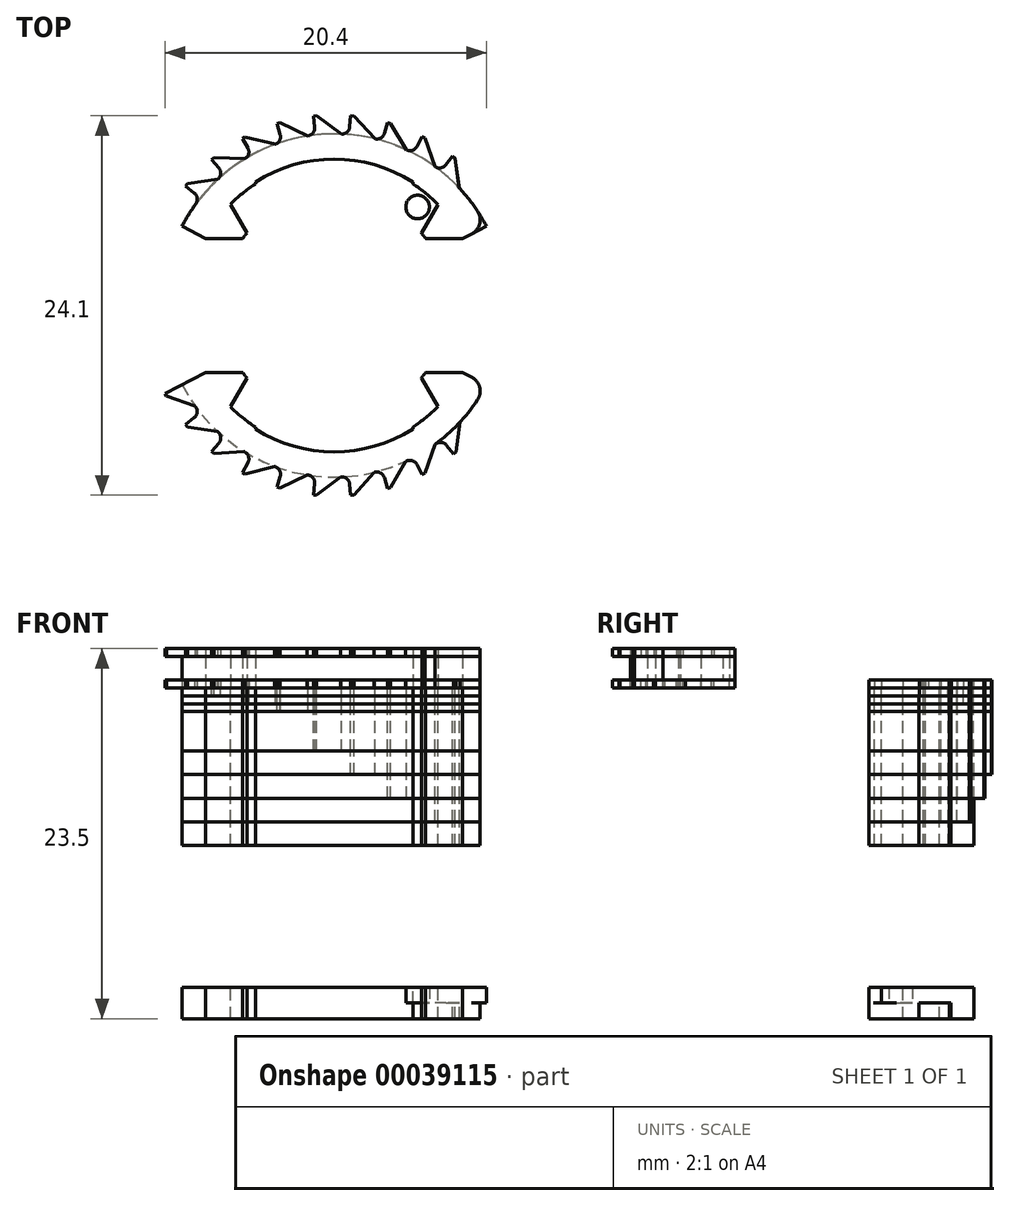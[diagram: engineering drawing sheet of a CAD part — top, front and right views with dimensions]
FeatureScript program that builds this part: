
annotation { "Feature Type Name" : "Feature", "Feature Type Description" : "" }
export const myFeature = defineFeature(function(context is Context, id is Id, definition is map)
    precondition{}
    {
        {
            var Q0;
            Q0=qCreatedBy(makeId("Top.planeOp"),FACE);
            var sketch = newSketch(context, id + "F0", { "sketchPlane" : qUnion([Q0])});
            skArc(sketch, "E0", {"start": v(6.4, -8.83) * mm, "mid": v(-2.5, -10.6) * mm, "end": v(-9.67, -5.03) * mm});
            skArc(sketch, "E1", {"start": v(-5, -7.84) * mm, "mid": v(0, -9.3) * mm, "end": v(5, -7.84) * mm});
            skArc(sketch, "E2", {"start": v(6.6, -6.42) * mm, "mid": v(5.83, -7.12) * mm, "end": v(5, -7.72) * mm});
            skLineSegment(sketch, "E3", {"start": v(9.67, -5.03) * mm, "end": v(0, 0) * mm, "construction": true});
            skLineSegment(sketch, "E4", {"start": v(-9.67, -5.03) * mm, "end": v(0, 0) * mm, "construction": true});
            skLineSegment(sketch, "E5", {"start": v(5, -7.84) * mm, "end": v(5, -7.72) * mm});
            skLineSegment(sketch, "E6", {"start": v(-5, -7.84) * mm, "end": v(-5, -7.72) * mm});
            skArc(sketch, "E7.trimOffspring", {"start": v(-5, -7.72) * mm, "mid": v(-5.83, -7.12) * mm, "end": v(-6.6, -6.42) * mm});
            skArc(sketch, "E8", {"start": v(-6.15, -3.75) * mm, "mid": v(0.86, -7.15) * mm, "end": v(6.86, -2.18) * mm, "construction": true});
            skLineSegment(sketch, "E9", {"start": v(-6.6, -6.42) * mm, "end": v(-5.54, -4.6) * mm});
            skLineSegment(sketch, "E10", {"start": v(6.6, -6.42) * mm, "end": v(5.54, -4.6) * mm});
            skArc(sketch, "E11", {"start": v(-5.54, -4.6) * mm, "mid": v(-5.68, -4.43) * mm, "end": v(-5.81, -4.25) * mm});
            skLineSegment(sketch, "E12", {"start": v(-5.81, -4.25) * mm, "end": v(-8.16, -4.25) * mm});
            skLineSegment(sketch, "E13", {"start": v(-8.16, -4.25) * mm, "end": v(-9.67, -5.03) * mm});
            skArc(sketch, "E14", {"start": v(5.54, -4.6) * mm, "mid": v(5.68, -4.43) * mm, "end": v(5.81, -4.25) * mm});
            skLineSegment(sketch, "E15", {"start": v(5.81, -4.25) * mm, "end": v(8.16, -4.25) * mm});
            skLineSegment(sketch, "E16", {"start": v(8.16, -4.25) * mm, "end": v(8.74, -4.55) * mm});
            skPoint(sketch, "E17.visualSharp", {"position": v(9.67, -5.03) * mm});
            skArc(sketch, "E17.filletArc", {"start": v(9.11, -5.98) * mm, "mid": v(9.24, -5.18) * mm, "end": v(8.74, -4.55) * mm});
            skPoint(sketch, "E18.visualSharp", {"position": v(-9.67, -5.03) * mm});
            skLineSegment(sketch, "E19", {"start": v(5.26, -10.1) * mm, "end": v(5.59, -10.73) * mm});
            skLineSegment(sketch, "E20", {"start": v(5.59, -10.73) * mm, "end": v(5.76, -10.64) * mm});
            skLineSegment(sketch, "E21", {"start": v(5.76, -10.64) * mm, "end": v(6.4, -8.83) * mm});
            skLineSegment(sketch, "E22", {"start": v(6.4, -8.83) * mm, "end": v(7.12, -9.83) * mm, "construction": true});
            skPoint(sketch, "E23.newPointA", {"position": v(5.03, -9.67) * mm});
            skArc(sketch, "E23.filletArc", {"start": v(5.26, -10.1) * mm, "mid": v(4.98, -9.86) * mm, "end": v(4.6, -9.88) * mm});
            skArc(sketch, "E24", {"start": v(9.11, -5.98) * mm, "mid": v(7.88, -7.53) * mm, "end": v(6.4, -8.83) * mm});
            skSolve(sketch);
        }
        {
            var Q0;
            Q0 = qSketchRegion(id + "F0", true);
            extrude(context, id + "F1", {"entities" : qUnion([Q0]), "depth" : 1.5 * mm});
        }
        {
            var Q0;
            Q0=makeQuery(id+"F1.opExtrude","SWEPT_BODY",BODY,{"disambiguationData":[OSD([sQuery(id+"F0.wireOp",EDGE,"E0"),sQuery(id+"F0.wireOp",EDGE,"E1"),sQuery(id+"F0.wireOp",EDGE,"E2"),sQuery(id+"F0.wireOp",EDGE,"E5"),sQuery(id+"F0.wireOp",EDGE,"E6"),sQuery(id+"F0.wireOp",EDGE,"E7.trimOffspring"),sQuery(id+"F0.wireOp",EDGE,"E9"),sQuery(id+"F0.wireOp",EDGE,"E10"),sQuery(id+"F0.wireOp",EDGE,"E11"),sQuery(id+"F0.wireOp",EDGE,"E12"),sQuery(id+"F0.wireOp",EDGE,"E13"),sQuery(id+"F0.wireOp",EDGE,"E14"),sQuery(id+"F0.wireOp",EDGE,"E15"),sQuery(id+"F0.wireOp",EDGE,"E16"),sQuery(id+"F0.wireOp",EDGE,"E17.filletArc"),sQuery(id+"F0.wireOp",EDGE,"E19"),sQuery(id+"F0.wireOp",EDGE,"E20"),sQuery(id+"F0.wireOp",EDGE,"E21"),sQuery(id+"F0.wireOp",EDGE,"E23.filletArc"),sQuery(id+"F0.wireOp",EDGE,"E24")])]});
            transform(context, id + "F2", {"entities" : qUnion([Q0]), "transformType" : TransformType.TRANSLATION_3D, "dx" : 0 * mm, "dy" : 0 * mm, "dz" : 0.5 * mm, "makeCopy" : true});
        }
        {
            var Q0;
            Q0=makeQuery(id+"F2.opPattern","COPY",BODY,{"derivedFrom":makeQuery(id+"F1.opExtrude","SWEPT_BODY",BODY,{"disambiguationData":[OSD([sQuery(id+"F0.wireOp",EDGE,"E0"),sQuery(id+"F0.wireOp",EDGE,"E1"),sQuery(id+"F0.wireOp",EDGE,"E2"),sQuery(id+"F0.wireOp",EDGE,"E5"),sQuery(id+"F0.wireOp",EDGE,"E6"),sQuery(id+"F0.wireOp",EDGE,"E7.trimOffspring"),sQuery(id+"F0.wireOp",EDGE,"E9"),sQuery(id+"F0.wireOp",EDGE,"E10"),sQuery(id+"F0.wireOp",EDGE,"E11"),sQuery(id+"F0.wireOp",EDGE,"E12"),sQuery(id+"F0.wireOp",EDGE,"E13"),sQuery(id+"F0.wireOp",EDGE,"E14"),sQuery(id+"F0.wireOp",EDGE,"E15"),sQuery(id+"F0.wireOp",EDGE,"E16"),sQuery(id+"F0.wireOp",EDGE,"E17.filletArc"),sQuery(id+"F0.wireOp",EDGE,"E19"),sQuery(id+"F0.wireOp",EDGE,"E20"),sQuery(id+"F0.wireOp",EDGE,"E21"),sQuery(id+"F0.wireOp",EDGE,"E23.filletArc"),sQuery(id+"F0.wireOp",EDGE,"E24")])]}),"instanceName":"1"});
            deleteBodies(context, id + "F3", {"entities" : qUnion([Q0])});
        }
        {
            var Q0;
            Q0=makeQuery(id+"F1.opExtrude","CAP_FACE",FACE,{"disambiguationData":[OSD([sQuery(id+"F0.wireOp",EDGE,"E0"),sQuery(id+"F0.wireOp",EDGE,"E1"),sQuery(id+"F0.wireOp",EDGE,"E2"),sQuery(id+"F0.wireOp",EDGE,"E5"),sQuery(id+"F0.wireOp",EDGE,"E6"),sQuery(id+"F0.wireOp",EDGE,"E7.trimOffspring"),sQuery(id+"F0.wireOp",EDGE,"E9"),sQuery(id+"F0.wireOp",EDGE,"E10"),sQuery(id+"F0.wireOp",EDGE,"E11"),sQuery(id+"F0.wireOp",EDGE,"E12"),sQuery(id+"F0.wireOp",EDGE,"E13"),sQuery(id+"F0.wireOp",EDGE,"E14"),sQuery(id+"F0.wireOp",EDGE,"E15"),sQuery(id+"F0.wireOp",EDGE,"E16"),sQuery(id+"F0.wireOp",EDGE,"E17.filletArc"),sQuery(id+"F0.wireOp",EDGE,"E19"),sQuery(id+"F0.wireOp",EDGE,"E20"),sQuery(id+"F0.wireOp",EDGE,"E21"),sQuery(id+"F0.wireOp",EDGE,"E23.filletArc"),sQuery(id+"F0.wireOp",EDGE,"E24")])],"isStart":false});
            var sketch = newSketch(context, id + "F4", { "sketchPlane" : qUnion([Q0])});
            skArc(sketch, "E25", {"start": v(6.4, -8.83) * mm, "mid": v(-2.5, -10.6) * mm, "end": v(-9.67, -5.03) * mm});
            skArc(sketch, "E26", {"start": v(-5, -7.84) * mm, "mid": v(0, -9.3) * mm, "end": v(5, -7.84) * mm});
            skArc(sketch, "E27", {"start": v(6.6, -6.42) * mm, "mid": v(5.83, -7.12) * mm, "end": v(5, -7.72) * mm});
            skLineSegment(sketch, "E28", {"start": v(0, 0) * mm, "end": v(-9.67, 5.03) * mm, "construction": true});
            skLineSegment(sketch, "E29", {"start": v(-9.67, -5.03) * mm, "end": v(0, 0) * mm, "construction": true});
            skLineSegment(sketch, "E30", {"start": v(5, -7.84) * mm, "end": v(5, -7.72) * mm});
            skLineSegment(sketch, "E31", {"start": v(-5, -7.84) * mm, "end": v(-5, -7.72) * mm});
            skArc(sketch, "E32.trimOffspring", {"start": v(-5, -7.72) * mm, "mid": v(-5.83, -7.12) * mm, "end": v(-6.6, -6.42) * mm});
            skArc(sketch, "E33", {"start": v(-6.15, -3.75) * mm, "mid": v(0.86, -7.15) * mm, "end": v(6.86, -2.18) * mm, "construction": true});
            skLineSegment(sketch, "E34", {"start": v(-6.6, -6.42) * mm, "end": v(-5.54, -4.6) * mm});
            skLineSegment(sketch, "E35", {"start": v(6.6, -6.42) * mm, "end": v(5.54, -4.6) * mm});
            skArc(sketch, "E36", {"start": v(-5.54, -4.6) * mm, "mid": v(-5.68, -4.43) * mm, "end": v(-5.81, -4.25) * mm});
            skLineSegment(sketch, "E37", {"start": v(-5.81, -4.25) * mm, "end": v(-8.16, -4.25) * mm});
            skLineSegment(sketch, "E38", {"start": v(-8.16, -4.25) * mm, "end": v(-9.67, -5.03) * mm});
            skArc(sketch, "E39", {"start": v(5.54, -4.6) * mm, "mid": v(5.68, -4.43) * mm, "end": v(5.81, -4.25) * mm});
            skLineSegment(sketch, "E40", {"start": v(5.81, -4.25) * mm, "end": v(8.16, -4.25) * mm});
            skLineSegment(sketch, "E41", {"start": v(8.16, -4.25) * mm, "end": v(8.74, -4.55) * mm});
            skPoint(sketch, "E42.visualSharp", {"position": v(-9.67, 5.03) * mm});
            skArc(sketch, "E42.filletArc", {"start": v(9.11, -5.98) * mm, "mid": v(9.24, -5.18) * mm, "end": v(8.74, -4.55) * mm});
            skPoint(sketch, "E43.visualSharp", {"position": v(-9.67, -5.03) * mm});
            skLineSegment(sketch, "E44", {"start": v(5.26, -10.1) * mm, "end": v(5.59, -10.73) * mm});
            skLineSegment(sketch, "E45", {"start": v(5.59, -10.73) * mm, "end": v(5.76, -10.64) * mm});
            skLineSegment(sketch, "E46", {"start": v(5.76, -10.64) * mm, "end": v(6.4, -8.83) * mm});
            skLineSegment(sketch, "E47", {"start": v(6.4, -8.83) * mm, "end": v(7.12, -9.83) * mm, "construction": true});
            skPoint(sketch, "E48.newPointA", {"position": v(5.03, -9.67) * mm});
            skArc(sketch, "E48.filletArc", {"start": v(5.26, -10.1) * mm, "mid": v(4.98, -9.86) * mm, "end": v(4.6, -9.88) * mm});
            skArc(sketch, "E49", {"start": v(9.11, -5.98) * mm, "mid": v(7.88, -7.53) * mm, "end": v(6.4, -8.83) * mm});
            skArc(sketch, "E50.1.0", {"start": v(3.19, -10.93) * mm, "mid": v(2.96, -10.64) * mm, "end": v(2.59, -10.59) * mm});
            skLineSegment(sketch, "E50.1.1", {"start": v(3.19, -10.93) * mm, "end": v(3.39, -11.62) * mm});
            skLineSegment(sketch, "E50.1.2", {"start": v(3.39, -11.62) * mm, "end": v(3.58, -11.56) * mm});
            skLineSegment(sketch, "E50.1.3", {"start": v(3.58, -11.56) * mm, "end": v(4.55, -9.9) * mm});
            skArc(sketch, "E50.2.0", {"start": v(1, -11.35) * mm, "mid": v(0.82, -11.01) * mm, "end": v(0.47, -10.89) * mm});
            skLineSegment(sketch, "E50.2.1", {"start": v(1, -11.35) * mm, "end": v(1.05, -12.05) * mm});
            skLineSegment(sketch, "E50.2.2", {"start": v(1.05, -12.05) * mm, "end": v(1.25, -12.04) * mm});
            skLineSegment(sketch, "E50.2.3", {"start": v(1.25, -12.04) * mm, "end": v(2.53, -10.6) * mm});
            skArc(sketch, "E50.3.0", {"start": v(-1.24, -11.32) * mm, "mid": v(-1.34, -10.96) * mm, "end": v(-1.66, -10.77) * mm});
            skLineSegment(sketch, "E50.3.1", {"start": v(-1.24, -11.32) * mm, "end": v(-1.32, -12.03) * mm});
            skLineSegment(sketch, "E50.3.2", {"start": v(-1.32, -12.03) * mm, "end": v(-1.12, -12.05) * mm});
            skLineSegment(sketch, "E50.3.3", {"start": v(-1.12, -12.05) * mm, "end": v(0.4, -10.9) * mm});
            skArc(sketch, "E50.4.0", {"start": v(-3.42, -10.86) * mm, "mid": v(-3.45, -10.5) * mm, "end": v(-3.73, -10.24) * mm});
            skLineSegment(sketch, "E50.4.1", {"start": v(-3.42, -10.86) * mm, "end": v(-3.64, -11.54) * mm});
            skLineSegment(sketch, "E50.4.2", {"start": v(-3.64, -11.54) * mm, "end": v(-3.45, -11.6) * mm});
            skLineSegment(sketch, "E50.4.3", {"start": v(-3.45, -11.6) * mm, "end": v(-1.72, -10.76) * mm});
            skArc(sketch, "E50.5.0", {"start": v(-5.48, -9.99) * mm, "mid": v(-5.43, -9.62) * mm, "end": v(-5.66, -9.32) * mm});
            skLineSegment(sketch, "E50.5.1", {"start": v(-5.48, -9.99) * mm, "end": v(-5.82, -10.6) * mm});
            skLineSegment(sketch, "E50.5.2", {"start": v(-5.82, -10.6) * mm, "end": v(-5.64, -10.7) * mm});
            skLineSegment(sketch, "E50.5.3", {"start": v(-5.64, -10.7) * mm, "end": v(-3.8, -10.22) * mm});
            skArc(sketch, "E50.6.0", {"start": v(-7.32, -8.72) * mm, "mid": v(-7.2, -8.37) * mm, "end": v(-7.37, -8.03) * mm});
            skLineSegment(sketch, "E50.6.1", {"start": v(-7.32, -8.72) * mm, "end": v(-7.78, -9.27) * mm});
            skLineSegment(sketch, "E50.6.2", {"start": v(-7.78, -9.27) * mm, "end": v(-7.62, -9.4) * mm});
            skLineSegment(sketch, "E50.6.3", {"start": v(-7.62, -9.4) * mm, "end": v(-5.71, -9.28) * mm});
            skArc(sketch, "E50.7.0", {"start": v(-8.88, -7.13) * mm, "mid": v(-8.7, -6.8) * mm, "end": v(-8.8, -6.44) * mm});
            skLineSegment(sketch, "E50.7.1", {"start": v(-8.88, -7.13) * mm, "end": v(-9.44, -7.57) * mm});
            skLineSegment(sketch, "E50.7.2", {"start": v(-9.44, -7.57) * mm, "end": v(-9.31, -7.73) * mm});
            skLineSegment(sketch, "E50.7.3", {"start": v(-9.31, -7.73) * mm, "end": v(-7.41, -8) * mm});
            skLineSegment(sketch, "E50.8.1", {"start": v(-10.1, -5.26) * mm, "end": v(-10.73, -5.59) * mm});
            skLineSegment(sketch, "E50.8.2", {"start": v(-10.73, -5.59) * mm, "end": v(-10.64, -5.76) * mm});
            skLineSegment(sketch, "E50.8.3", {"start": v(-10.64, -5.76) * mm, "end": v(-8.83, -6.4) * mm});
            skLineSegment(sketch, "E50.anchor1", {"start": v(0, 0) * mm, "end": v(4.82, -10.33) * mm, "construction": true});
            skLineSegment(sketch, "E50.anchor2", {"start": v(0, 0) * mm, "end": v(-10.33, -4.82) * mm, "construction": true});
            skLineSegment(sketch, "E51", {"start": v(-10.1, -5.26) * mm, "end": v(-9.67, -5.03) * mm});
            skSolve(sketch);
        }
        {
            var Q0;
            Q0=makeQuery(id+"F4.imprint","IMPRINT",FACE,{"disambiguationData":[TD([[makeQuery(id+"F4.imprint","IMPRINT",EDGE,{"derivedFrom":sQuery(id+"F4.wireOp",EDGE,"E44")}),1.0]])]});
            var Q1;
            {var subQ2=sQuery(id+"F4.wireOp",EDGE,"E50.1.0");Q1=makeQuery(id+"F4.imprint","IMPRINT",FACE,{"disambiguationData":[TD([[makeQuery(id+"F4.imprint","IMPRINT",EDGE,{"derivedFrom":subQ2}),-1.0]])]});}
            var Q2;
            {var subQ2=sQuery(id+"F4.wireOp",EDGE,"E50.2.0");Q2=makeQuery(id+"F4.imprint","IMPRINT",FACE,{"disambiguationData":[TD([[makeQuery(id+"F4.imprint","IMPRINT",EDGE,{"derivedFrom":subQ2}),-1.0]])]});}
            var Q3;
            {var subQ2=sQuery(id+"F4.wireOp",EDGE,"E50.3.0");Q3=makeQuery(id+"F4.imprint","IMPRINT",FACE,{"disambiguationData":[TD([[makeQuery(id+"F4.imprint","IMPRINT",EDGE,{"derivedFrom":subQ2}),-1.0]])]});}
            var Q4;
            {var subQ2=sQuery(id+"F4.wireOp",EDGE,"E50.4.0");Q4=makeQuery(id+"F4.imprint","IMPRINT",FACE,{"disambiguationData":[TD([[makeQuery(id+"F4.imprint","IMPRINT",EDGE,{"derivedFrom":subQ2}),-1.0]])]});}
            var Q5;
            {var subQ2=sQuery(id+"F4.wireOp",EDGE,"E50.5.0");Q5=makeQuery(id+"F4.imprint","IMPRINT",FACE,{"disambiguationData":[TD([[makeQuery(id+"F4.imprint","IMPRINT",EDGE,{"derivedFrom":subQ2}),-1.0]])]});}
            var Q6;
            {var subQ2=sQuery(id+"F4.wireOp",EDGE,"E50.6.0");Q6=makeQuery(id+"F4.imprint","IMPRINT",FACE,{"disambiguationData":[TD([[makeQuery(id+"F4.imprint","IMPRINT",EDGE,{"derivedFrom":subQ2}),-1.0]])]});}
            var Q7;
            {var subQ2=sQuery(id+"F4.wireOp",EDGE,"E50.7.0");Q7=makeQuery(id+"F4.imprint","IMPRINT",FACE,{"disambiguationData":[TD([[makeQuery(id+"F4.imprint","IMPRINT",EDGE,{"derivedFrom":subQ2}),-1.0]])]});}
            var Q8;
            Q8=makeQuery(id+"F4.imprint","IMPRINT",FACE,{"disambiguationData":[TD([[makeQuery(id+"F4.imprint","IMPRINT",EDGE,{"derivedFrom":sQuery(id+"F4.wireOp",EDGE,"E50.8.1")}),1.0]])]});
            var Q9;
            Q9=makeQuery(id+"F4.imprint","IMPRINT",FACE,{"disambiguationData":[TD([[makeQuery(id+"F4.imprint","IMPRINT",EDGE,{"derivedFrom":sQuery(id+"F4.wireOp",EDGE,"E26")}),-1.0]])]});
            extrude(context, id + "F5", {"entities" : qUnion([Q0, Q1, Q2, Q3, Q4, Q5, Q6, Q7, Q8, Q9]), "depth" : 0.5 * mm});
        }
        {
            var Q0;
            Q0=qCreatedBy(makeId("Top.planeOp"),FACE);
            var sketch = newSketch(context, id + "F6", { "sketchPlane" : qUnion([Q0])});
            skArc(sketch, "E52", {"start": v(6.4, -8.83) * mm, "mid": v(-2.5, -10.6) * mm, "end": v(-9.67, -5.03) * mm});
            skArc(sketch, "E53", {"start": v(-5, -7.84) * mm, "mid": v(0, -9.3) * mm, "end": v(5, -7.84) * mm});
            skArc(sketch, "E54", {"start": v(6.6, -6.42) * mm, "mid": v(5.83, -7.12) * mm, "end": v(5, -7.72) * mm});
            skLineSegment(sketch, "E55", {"start": v(0, 0) * mm, "end": v(-9.67, 5.03) * mm, "construction": true});
            skLineSegment(sketch, "E56", {"start": v(-9.67, -5.03) * mm, "end": v(0, 0) * mm, "construction": true});
            skLineSegment(sketch, "E57", {"start": v(5, -7.84) * mm, "end": v(5, -7.72) * mm});
            skLineSegment(sketch, "E58", {"start": v(-5, -7.84) * mm, "end": v(-5, -7.72) * mm});
            skArc(sketch, "E59.trimOffspring", {"start": v(-5, -7.72) * mm, "mid": v(-5.83, -7.12) * mm, "end": v(-6.6, -6.42) * mm});
            skArc(sketch, "E60", {"start": v(-6.15, -3.75) * mm, "mid": v(0.86, -7.15) * mm, "end": v(6.86, -2.18) * mm, "construction": true});
            skLineSegment(sketch, "E61", {"start": v(-6.6, -6.42) * mm, "end": v(-5.54, -4.6) * mm});
            skLineSegment(sketch, "E62", {"start": v(6.6, -6.42) * mm, "end": v(5.54, -4.6) * mm});
            skArc(sketch, "E63", {"start": v(-5.54, -4.6) * mm, "mid": v(-5.68, -4.43) * mm, "end": v(-5.81, -4.25) * mm});
            skLineSegment(sketch, "E64", {"start": v(-5.81, -4.25) * mm, "end": v(-8.16, -4.25) * mm});
            skLineSegment(sketch, "E65", {"start": v(-8.16, -4.25) * mm, "end": v(-9.67, -5.03) * mm});
            skArc(sketch, "E66", {"start": v(5.54, -4.6) * mm, "mid": v(5.68, -4.43) * mm, "end": v(5.81, -4.25) * mm});
            skLineSegment(sketch, "E67", {"start": v(5.81, -4.25) * mm, "end": v(8.16, -4.25) * mm});
            skLineSegment(sketch, "E68", {"start": v(8.16, -4.25) * mm, "end": v(8.74, -4.55) * mm});
            skPoint(sketch, "E69.visualSharp", {"position": v(-9.67, 5.03) * mm});
            skArc(sketch, "E69.filletArc", {"start": v(9.11, -5.98) * mm, "mid": v(9.24, -5.18) * mm, "end": v(8.74, -4.55) * mm});
            skPoint(sketch, "E70.visualSharp", {"position": v(-9.67, -5.03) * mm});
            skLineSegment(sketch, "E71", {"start": v(5.26, -10.1) * mm, "end": v(5.59, -10.73) * mm});
            skLineSegment(sketch, "E72", {"start": v(5.59, -10.73) * mm, "end": v(5.76, -10.64) * mm});
            skLineSegment(sketch, "E73", {"start": v(5.76, -10.64) * mm, "end": v(6.4, -8.83) * mm});
            skLineSegment(sketch, "E74", {"start": v(6.4, -8.83) * mm, "end": v(7.12, -9.83) * mm, "construction": true});
            skPoint(sketch, "E75.newPointA", {"position": v(5.03, -9.67) * mm});
            skArc(sketch, "E75.filletArc", {"start": v(5.26, -10.1) * mm, "mid": v(4.98, -9.86) * mm, "end": v(4.6, -9.88) * mm});
            skArc(sketch, "E76", {"start": v(9.11, -5.98) * mm, "mid": v(7.88, -7.53) * mm, "end": v(6.4, -8.83) * mm});
            skArc(sketch, "E77.1.0", {"start": v(3.19, -10.93) * mm, "mid": v(2.96, -10.64) * mm, "end": v(2.59, -10.59) * mm});
            skLineSegment(sketch, "E77.1.1", {"start": v(3.19, -10.93) * mm, "end": v(3.39, -11.62) * mm});
            skLineSegment(sketch, "E77.1.2", {"start": v(3.39, -11.62) * mm, "end": v(3.58, -11.56) * mm});
            skLineSegment(sketch, "E77.1.3", {"start": v(3.58, -11.56) * mm, "end": v(4.55, -9.9) * mm});
            skArc(sketch, "E77.2.0", {"start": v(1, -11.35) * mm, "mid": v(0.82, -11.01) * mm, "end": v(0.47, -10.89) * mm});
            skLineSegment(sketch, "E77.2.1", {"start": v(1, -11.35) * mm, "end": v(1.05, -12.05) * mm});
            skLineSegment(sketch, "E77.2.2", {"start": v(1.05, -12.05) * mm, "end": v(1.25, -12.04) * mm});
            skLineSegment(sketch, "E77.2.3", {"start": v(1.25, -12.04) * mm, "end": v(2.53, -10.6) * mm});
            skArc(sketch, "E77.3.0", {"start": v(-1.24, -11.32) * mm, "mid": v(-1.34, -10.96) * mm, "end": v(-1.66, -10.77) * mm});
            skLineSegment(sketch, "E77.3.1", {"start": v(-1.24, -11.32) * mm, "end": v(-1.32, -12.03) * mm});
            skLineSegment(sketch, "E77.3.2", {"start": v(-1.32, -12.03) * mm, "end": v(-1.12, -12.05) * mm});
            skLineSegment(sketch, "E77.3.3", {"start": v(-1.12, -12.05) * mm, "end": v(0.4, -10.9) * mm});
            skArc(sketch, "E77.4.0", {"start": v(-3.42, -10.86) * mm, "mid": v(-3.45, -10.5) * mm, "end": v(-3.73, -10.24) * mm});
            skLineSegment(sketch, "E77.4.1", {"start": v(-3.42, -10.86) * mm, "end": v(-3.64, -11.54) * mm});
            skLineSegment(sketch, "E77.4.2", {"start": v(-3.64, -11.54) * mm, "end": v(-3.45, -11.6) * mm});
            skLineSegment(sketch, "E77.4.3", {"start": v(-3.45, -11.6) * mm, "end": v(-1.72, -10.76) * mm});
            skArc(sketch, "E77.5.0", {"start": v(-5.48, -9.99) * mm, "mid": v(-5.43, -9.62) * mm, "end": v(-5.66, -9.32) * mm});
            skLineSegment(sketch, "E77.5.1", {"start": v(-5.48, -9.99) * mm, "end": v(-5.82, -10.6) * mm});
            skLineSegment(sketch, "E77.5.2", {"start": v(-5.82, -10.6) * mm, "end": v(-5.64, -10.7) * mm});
            skLineSegment(sketch, "E77.5.3", {"start": v(-5.64, -10.7) * mm, "end": v(-3.8, -10.22) * mm});
            skArc(sketch, "E77.6.0", {"start": v(-7.32, -8.72) * mm, "mid": v(-7.2, -8.37) * mm, "end": v(-7.37, -8.03) * mm});
            skLineSegment(sketch, "E77.6.1", {"start": v(-7.32, -8.72) * mm, "end": v(-7.78, -9.27) * mm});
            skLineSegment(sketch, "E77.6.2", {"start": v(-7.78, -9.27) * mm, "end": v(-7.62, -9.4) * mm});
            skLineSegment(sketch, "E77.6.3", {"start": v(-7.62, -9.4) * mm, "end": v(-5.71, -9.28) * mm});
            skArc(sketch, "E77.7.0", {"start": v(-8.88, -7.13) * mm, "mid": v(-8.7, -6.8) * mm, "end": v(-8.8, -6.44) * mm});
            skLineSegment(sketch, "E77.7.1", {"start": v(-8.88, -7.13) * mm, "end": v(-9.44, -7.57) * mm});
            skLineSegment(sketch, "E77.7.2", {"start": v(-9.44, -7.57) * mm, "end": v(-9.31, -7.73) * mm});
            skLineSegment(sketch, "E77.7.3", {"start": v(-9.31, -7.73) * mm, "end": v(-7.41, -8) * mm});
            skLineSegment(sketch, "E77.8.1", {"start": v(-10.1, -5.26) * mm, "end": v(-10.73, -5.59) * mm});
            skLineSegment(sketch, "E77.8.2", {"start": v(-10.73, -5.59) * mm, "end": v(-10.64, -5.76) * mm});
            skLineSegment(sketch, "E77.8.3", {"start": v(-10.64, -5.76) * mm, "end": v(-8.83, -6.4) * mm});
            skLineSegment(sketch, "E77.anchor1", {"start": v(0, 0) * mm, "end": v(4.82, -10.33) * mm, "construction": true});
            skLineSegment(sketch, "E77.anchor2", {"start": v(0, 0) * mm, "end": v(-10.33, -4.82) * mm, "construction": true});
            skLineSegment(sketch, "E78", {"start": v(-10.1, -5.26) * mm, "end": v(-9.67, -5.03) * mm});
            skArc(sketch, "E79.1.0", {"start": v(7.13, -8.88) * mm, "mid": v(6.8, -8.7) * mm, "end": v(6.44, -8.8) * mm});
            skLineSegment(sketch, "E79.1.1", {"start": v(7.13, -8.88) * mm, "end": v(7.57, -9.44) * mm});
            skLineSegment(sketch, "E79.1.2", {"start": v(7.73, -9.31) * mm, "end": v(8, -7.41) * mm});
            skLineSegment(sketch, "E79.1.3", {"start": v(7.57, -9.44) * mm, "end": v(7.73, -9.31) * mm});
            skLineSegment(sketch, "E79.anchor2", {"start": v(0, 0) * mm, "end": v(6.74, -9.2) * mm, "construction": true});
            skSolve(sketch);
        }
        {
            var Q0;
            Q0 = qSketchRegion(id + "F6", true);
            extrude(context, id + "F7", {"entities" : qUnion([Q0]), "oppositeDirection" : true, "depth" : 0.5 * mm});
        }
        {
            var Q0;
            Q0=makeQuery(id+"F7.opExtrude","CAP_FACE",FACE,{"disambiguationData":[OSD([sQuery(id+"F6.wireOp",EDGE,"E52"),sQuery(id+"F6.wireOp",EDGE,"E53"),sQuery(id+"F6.wireOp",EDGE,"E54"),sQuery(id+"F6.wireOp",EDGE,"E57"),sQuery(id+"F6.wireOp",EDGE,"E58"),sQuery(id+"F6.wireOp",EDGE,"E59.trimOffspring"),sQuery(id+"F6.wireOp",EDGE,"E61"),sQuery(id+"F6.wireOp",EDGE,"E62"),sQuery(id+"F6.wireOp",EDGE,"E63"),sQuery(id+"F6.wireOp",EDGE,"E64"),sQuery(id+"F6.wireOp",EDGE,"E65"),sQuery(id+"F6.wireOp",EDGE,"E66"),sQuery(id+"F6.wireOp",EDGE,"E67"),sQuery(id+"F6.wireOp",EDGE,"E68"),sQuery(id+"F6.wireOp",EDGE,"E69.filletArc"),sQuery(id+"F6.wireOp",EDGE,"E71"),sQuery(id+"F6.wireOp",EDGE,"E72"),sQuery(id+"F6.wireOp",EDGE,"E73"),sQuery(id+"F6.wireOp",EDGE,"E75.filletArc"),sQuery(id+"F6.wireOp",EDGE,"E76"),sQuery(id+"F6.wireOp",EDGE,"E77.1.0"),sQuery(id+"F6.wireOp",EDGE,"E77.1.1"),sQuery(id+"F6.wireOp",EDGE,"E77.1.2"),sQuery(id+"F6.wireOp",EDGE,"E77.1.3"),sQuery(id+"F6.wireOp",EDGE,"E77.2.0"),sQuery(id+"F6.wireOp",EDGE,"E77.2.1"),sQuery(id+"F6.wireOp",EDGE,"E77.2.2"),sQuery(id+"F6.wireOp",EDGE,"E77.2.3"),sQuery(id+"F6.wireOp",EDGE,"E77.3.0"),sQuery(id+"F6.wireOp",EDGE,"E77.3.1"),sQuery(id+"F6.wireOp",EDGE,"E77.3.2"),sQuery(id+"F6.wireOp",EDGE,"E77.3.3"),sQuery(id+"F6.wireOp",EDGE,"E77.4.0"),sQuery(id+"F6.wireOp",EDGE,"E77.4.1"),sQuery(id+"F6.wireOp",EDGE,"E77.4.2"),sQuery(id+"F6.wireOp",EDGE,"E77.4.3"),sQuery(id+"F6.wireOp",EDGE,"E77.5.0"),sQuery(id+"F6.wireOp",EDGE,"E77.5.1"),sQuery(id+"F6.wireOp",EDGE,"E77.5.2"),sQuery(id+"F6.wireOp",EDGE,"E77.5.3"),sQuery(id+"F6.wireOp",EDGE,"E77.6.0"),sQuery(id+"F6.wireOp",EDGE,"E77.6.1"),sQuery(id+"F6.wireOp",EDGE,"E77.6.2"),sQuery(id+"F6.wireOp",EDGE,"E77.6.3"),sQuery(id+"F6.wireOp",EDGE,"E77.7.0"),sQuery(id+"F6.wireOp",EDGE,"E77.7.1"),sQuery(id+"F6.wireOp",EDGE,"E77.7.2"),sQuery(id+"F6.wireOp",EDGE,"E77.7.3"),sQuery(id+"F6.wireOp",EDGE,"E77.8.1"),sQuery(id+"F6.wireOp",EDGE,"E77.8.2"),sQuery(id+"F6.wireOp",EDGE,"E77.8.3"),sQuery(id+"F6.wireOp",EDGE,"E78"),sQuery(id+"F6.wireOp",EDGE,"E79.1.0"),sQuery(id+"F6.wireOp",EDGE,"E79.1.1"),sQuery(id+"F6.wireOp",EDGE,"E79.1.2"),sQuery(id+"F6.wireOp",EDGE,"E79.1.3")])],"isStart":false});
            var sketch = newSketch(context, id + "F8", { "sketchPlane" : qUnion([Q0])});
            skArc(sketch, "E80", {"start": v(6.4, -8.83) * mm, "mid": v(-2.5, -10.6) * mm, "end": v(-9.67, -5.03) * mm});
            skArc(sketch, "E81", {"start": v(-5, -7.84) * mm, "mid": v(0, -9.3) * mm, "end": v(5, -7.84) * mm});
            skArc(sketch, "E82", {"start": v(6.6, -6.42) * mm, "mid": v(5.83, -7.12) * mm, "end": v(5, -7.72) * mm});
            skLineSegment(sketch, "E83", {"start": v(0, 0) * mm, "end": v(-9.67, 5.03) * mm, "construction": true});
            skLineSegment(sketch, "E84", {"start": v(-9.67, -5.03) * mm, "end": v(0, 0) * mm, "construction": true});
            skLineSegment(sketch, "E85", {"start": v(5, -7.84) * mm, "end": v(5, -7.72) * mm});
            skLineSegment(sketch, "E86", {"start": v(-5, -7.84) * mm, "end": v(-5, -7.72) * mm});
            skArc(sketch, "E87.trimOffspring", {"start": v(-5, -7.72) * mm, "mid": v(-5.83, -7.12) * mm, "end": v(-6.6, -6.42) * mm});
            skArc(sketch, "E88", {"start": v(-6.15, -3.75) * mm, "mid": v(0.86, -7.15) * mm, "end": v(6.86, -2.18) * mm, "construction": true});
            skLineSegment(sketch, "E89", {"start": v(-6.6, -6.42) * mm, "end": v(-5.54, -4.6) * mm});
            skLineSegment(sketch, "E90", {"start": v(6.6, -6.42) * mm, "end": v(5.54, -4.6) * mm});
            skArc(sketch, "E91", {"start": v(-5.54, -4.6) * mm, "mid": v(-5.68, -4.43) * mm, "end": v(-5.81, -4.25) * mm});
            skLineSegment(sketch, "E92", {"start": v(-5.81, -4.25) * mm, "end": v(-8.16, -4.25) * mm});
            skLineSegment(sketch, "E93", {"start": v(-8.16, -4.25) * mm, "end": v(-9.67, -5.03) * mm});
            skArc(sketch, "E94", {"start": v(5.54, -4.6) * mm, "mid": v(5.68, -4.43) * mm, "end": v(5.81, -4.25) * mm});
            skLineSegment(sketch, "E95", {"start": v(5.81, -4.25) * mm, "end": v(8.16, -4.25) * mm});
            skLineSegment(sketch, "E96", {"start": v(8.16, -4.25) * mm, "end": v(8.74, -4.55) * mm});
            skPoint(sketch, "E97.visualSharp", {"position": v(-9.67, 5.03) * mm});
            skArc(sketch, "E97.filletArc", {"start": v(9.11, -5.98) * mm, "mid": v(9.24, -5.18) * mm, "end": v(8.74, -4.55) * mm});
            skPoint(sketch, "E98.visualSharp", {"position": v(-9.67, -5.03) * mm});
            skLineSegment(sketch, "E99", {"start": v(5.26, -10.1) * mm, "end": v(5.59, -10.73) * mm});
            skLineSegment(sketch, "E100", {"start": v(5.59, -10.73) * mm, "end": v(5.76, -10.64) * mm});
            skPoint(sketch, "E101.newPointA", {"position": v(5.03, -9.67) * mm});
            skArc(sketch, "E101.filletArc", {"start": v(5.26, -10.1) * mm, "mid": v(4.98, -9.86) * mm, "end": v(4.6, -9.88) * mm});
            skArc(sketch, "E102", {"start": v(9.11, -5.98) * mm, "mid": v(7.88, -7.53) * mm, "end": v(6.4, -8.83) * mm});
            skArc(sketch, "E103.1.0", {"start": v(3.19, -10.93) * mm, "mid": v(2.96, -10.64) * mm, "end": v(2.59, -10.59) * mm});
            skLineSegment(sketch, "E103.1.1", {"start": v(3.19, -10.93) * mm, "end": v(3.39, -11.62) * mm});
            skLineSegment(sketch, "E103.1.2", {"start": v(3.39, -11.62) * mm, "end": v(3.58, -11.56) * mm});
            skLineSegment(sketch, "E103.1.3", {"start": v(4.6, -9.88) * mm, "end": v(3.58, -11.56) * mm});
            skArc(sketch, "E103.2.0", {"start": v(1, -11.35) * mm, "mid": v(0.82, -11.01) * mm, "end": v(0.47, -10.89) * mm});
            skLineSegment(sketch, "E103.2.1", {"start": v(1, -11.35) * mm, "end": v(1.05, -12.05) * mm});
            skLineSegment(sketch, "E103.2.2", {"start": v(1.05, -12.05) * mm, "end": v(1.25, -12.04) * mm});
            skLineSegment(sketch, "E103.2.3", {"start": v(2.59, -10.59) * mm, "end": v(1.25, -12.04) * mm});
            skArc(sketch, "E103.3.0", {"start": v(-1.24, -11.32) * mm, "mid": v(-1.34, -10.96) * mm, "end": v(-1.66, -10.77) * mm});
            skLineSegment(sketch, "E103.3.1", {"start": v(-1.24, -11.32) * mm, "end": v(-1.32, -12.03) * mm});
            skLineSegment(sketch, "E103.3.2", {"start": v(-1.32, -12.03) * mm, "end": v(-1.12, -12.05) * mm});
            skLineSegment(sketch, "E103.3.3", {"start": v(0.47, -10.89) * mm, "end": v(-1.12, -12.05) * mm});
            skArc(sketch, "E103.4.0", {"start": v(-3.42, -10.86) * mm, "mid": v(-3.45, -10.5) * mm, "end": v(-3.73, -10.24) * mm});
            skLineSegment(sketch, "E103.4.1", {"start": v(-3.42, -10.86) * mm, "end": v(-3.64, -11.54) * mm});
            skLineSegment(sketch, "E103.4.2", {"start": v(-3.64, -11.54) * mm, "end": v(-3.45, -11.6) * mm});
            skLineSegment(sketch, "E103.4.3", {"start": v(-1.66, -10.77) * mm, "end": v(-3.45, -11.6) * mm});
            skArc(sketch, "E103.5.0", {"start": v(-5.48, -9.99) * mm, "mid": v(-5.43, -9.62) * mm, "end": v(-5.66, -9.32) * mm});
            skLineSegment(sketch, "E103.5.1", {"start": v(-5.48, -9.99) * mm, "end": v(-5.82, -10.6) * mm});
            skLineSegment(sketch, "E103.5.2", {"start": v(-5.82, -10.6) * mm, "end": v(-5.64, -10.7) * mm});
            skLineSegment(sketch, "E103.5.3", {"start": v(-3.73, -10.24) * mm, "end": v(-5.64, -10.7) * mm});
            skArc(sketch, "E103.6.0", {"start": v(-7.32, -8.72) * mm, "mid": v(-7.2, -8.37) * mm, "end": v(-7.37, -8.03) * mm});
            skLineSegment(sketch, "E103.6.1", {"start": v(-7.32, -8.72) * mm, "end": v(-7.78, -9.27) * mm});
            skLineSegment(sketch, "E103.6.2", {"start": v(-7.78, -9.27) * mm, "end": v(-7.62, -9.4) * mm});
            skLineSegment(sketch, "E103.6.3", {"start": v(-5.66, -9.32) * mm, "end": v(-7.62, -9.4) * mm});
            skArc(sketch, "E103.7.0", {"start": v(-8.88, -7.13) * mm, "mid": v(-8.7, -6.8) * mm, "end": v(-8.8, -6.44) * mm});
            skLineSegment(sketch, "E103.7.1", {"start": v(-8.88, -7.13) * mm, "end": v(-9.44, -7.57) * mm});
            skLineSegment(sketch, "E103.7.2", {"start": v(-9.44, -7.57) * mm, "end": v(-9.31, -7.73) * mm});
            skLineSegment(sketch, "E103.7.3", {"start": v(-7.37, -8.03) * mm, "end": v(-9.31, -7.73) * mm});
            skLineSegment(sketch, "E103.anchor1", {"start": v(0, 0) * mm, "end": v(4.82, -10.33) * mm, "construction": true});
            skLineSegment(sketch, "E103.anchor2", {"start": v(0, 0) * mm, "end": v(-10.33, -4.82) * mm, "construction": true});
            skLineSegment(sketch, "E104", {"start": v(6.4, -8.83) * mm, "end": v(7.19, -9.93) * mm, "construction": true});
            skLineSegment(sketch, "E105", {"start": v(5.76, -10.64) * mm, "end": v(6.4, -8.83) * mm});
            skArc(sketch, "E106.1.0", {"start": v(7.08, -8.92) * mm, "mid": v(6.75, -8.74) * mm, "end": v(6.4, -8.83) * mm});
            skLineSegment(sketch, "E106.1.1", {"start": v(7.08, -8.92) * mm, "end": v(7.52, -9.48) * mm});
            skLineSegment(sketch, "E106.1.2", {"start": v(7.52, -9.48) * mm, "end": v(7.68, -9.35) * mm});
            skLineSegment(sketch, "E106.1.3", {"start": v(7.68, -9.35) * mm, "end": v(7.95, -7.46) * mm});
            skPoint(sketch, "E106.center", {"position": v(0.04, -0.07) * mm});
            skLineSegment(sketch, "E106.anchor1", {"start": v(0.04, -0.07) * mm, "end": v(4.82, -10.33) * mm, "construction": true});
            skLineSegment(sketch, "E106.anchor2", {"start": v(0.04, -0.07) * mm, "end": v(6.69, -9.23) * mm, "construction": true});
            skSolve(sketch);
        }
        {
            var Q0;
            Q0=makeQuery(id+"F8.imprint","IMPRINT",FACE,{"disambiguationData":[TD([[makeQuery(id+"F8.imprint","IMPRINT",EDGE,{"derivedFrom":sQuery(id+"F8.wireOp",EDGE,"E99")}),1.0]])]});
            var Q1;
            {var subQ2=sQuery(id+"F8.wireOp",EDGE,"E103.1.0");Q1=makeQuery(id+"F8.imprint","IMPRINT",FACE,{"disambiguationData":[TD([[makeQuery(id+"F8.imprint","IMPRINT",EDGE,{"derivedFrom":subQ2}),-1.0]])]});}
            var Q2;
            {var subQ2=sQuery(id+"F8.wireOp",EDGE,"E103.2.0");Q2=makeQuery(id+"F8.imprint","IMPRINT",FACE,{"disambiguationData":[TD([[makeQuery(id+"F8.imprint","IMPRINT",EDGE,{"derivedFrom":subQ2}),-1.0]])]});}
            var Q3;
            {var subQ2=sQuery(id+"F8.wireOp",EDGE,"E103.3.0");Q3=makeQuery(id+"F8.imprint","IMPRINT",FACE,{"disambiguationData":[TD([[makeQuery(id+"F8.imprint","IMPRINT",EDGE,{"derivedFrom":subQ2}),-1.0]])]});}
            var Q4;
            {var subQ2=sQuery(id+"F8.wireOp",EDGE,"E103.4.0");Q4=makeQuery(id+"F8.imprint","IMPRINT",FACE,{"disambiguationData":[TD([[makeQuery(id+"F8.imprint","IMPRINT",EDGE,{"derivedFrom":subQ2}),-1.0]])]});}
            var Q5;
            {var subQ2=sQuery(id+"F8.wireOp",EDGE,"E103.5.0");Q5=makeQuery(id+"F8.imprint","IMPRINT",FACE,{"disambiguationData":[TD([[makeQuery(id+"F8.imprint","IMPRINT",EDGE,{"derivedFrom":subQ2}),-1.0]])]});}
            var Q6;
            {var subQ1=sQuery(id+"F8.wireOp",EDGE,"E103.6.0");Q6=makeQuery(id+"F8.imprint","IMPRINT",FACE,{"disambiguationData":[TD([[makeQuery(id+"F8.imprint","IMPRINT",EDGE,{"derivedFrom":subQ1}),-1.0]])]});}
            var Q7;
            {var subQ1=sQuery(id+"F8.wireOp",EDGE,"E103.7.0");Q7=makeQuery(id+"F8.imprint","IMPRINT",FACE,{"disambiguationData":[TD([[makeQuery(id+"F8.imprint","IMPRINT",EDGE,{"derivedFrom":subQ1}),-1.0]])]});}
            var Q8;
            {var subQ4=sQuery(id+"F8.wireOp",EDGE,"E106.1.0");Q8=makeQuery(id+"F8.imprint","IMPRINT",FACE,{"disambiguationData":[TD([[makeQuery(id+"F8.imprint","IMPRINT",EDGE,{"derivedFrom":subQ4}),-1.0]])]});}
            var Q9;
            Q9=makeQuery(id+"F8.imprint","IMPRINT",FACE,{"disambiguationData":[TD([[makeQuery(id+"F8.imprint","IMPRINT",EDGE,{"derivedFrom":sQuery(id+"F8.wireOp",EDGE,"E81")}),-1.0]])]});
            extrude(context, id + "F9", {"entities" : qUnion([Q0, Q1, Q2, Q3, Q4, Q5, Q6, Q7, Q8, Q9]), "oppositeDirection" : true, "depth" : 0.5 * mm});
        }
        {
            var Q0;
            Q0=makeQuery(id+"F9.opExtrude","CAP_FACE",FACE,{"disambiguationData":[OSD([sQuery(id+"F8.wireOp",EDGE,"E80"),sQuery(id+"F8.wireOp",EDGE,"E81"),sQuery(id+"F8.wireOp",EDGE,"E82"),sQuery(id+"F8.wireOp",EDGE,"E85"),sQuery(id+"F8.wireOp",EDGE,"E86"),sQuery(id+"F8.wireOp",EDGE,"E87.trimOffspring"),sQuery(id+"F8.wireOp",EDGE,"E89"),sQuery(id+"F8.wireOp",EDGE,"E90"),sQuery(id+"F8.wireOp",EDGE,"E91"),sQuery(id+"F8.wireOp",EDGE,"E92"),sQuery(id+"F8.wireOp",EDGE,"E93"),sQuery(id+"F8.wireOp",EDGE,"E94"),sQuery(id+"F8.wireOp",EDGE,"E95"),sQuery(id+"F8.wireOp",EDGE,"E96"),sQuery(id+"F8.wireOp",EDGE,"E97.filletArc"),sQuery(id+"F8.wireOp",EDGE,"E99"),sQuery(id+"F8.wireOp",EDGE,"E100"),sQuery(id+"F8.wireOp",EDGE,"E101.filletArc"),sQuery(id+"F8.wireOp",EDGE,"E102"),sQuery(id+"F8.wireOp",EDGE,"E103.1.0"),sQuery(id+"F8.wireOp",EDGE,"E103.1.1"),sQuery(id+"F8.wireOp",EDGE,"E103.1.2"),sQuery(id+"F8.wireOp",EDGE,"E103.1.3"),sQuery(id+"F8.wireOp",EDGE,"E103.2.0"),sQuery(id+"F8.wireOp",EDGE,"E103.2.1"),sQuery(id+"F8.wireOp",EDGE,"E103.2.2"),sQuery(id+"F8.wireOp",EDGE,"E103.2.3"),sQuery(id+"F8.wireOp",EDGE,"E103.3.0"),sQuery(id+"F8.wireOp",EDGE,"E103.3.1"),sQuery(id+"F8.wireOp",EDGE,"E103.3.2"),sQuery(id+"F8.wireOp",EDGE,"E103.3.3"),sQuery(id+"F8.wireOp",EDGE,"E103.4.0"),sQuery(id+"F8.wireOp",EDGE,"E103.4.1"),sQuery(id+"F8.wireOp",EDGE,"E103.4.2"),sQuery(id+"F8.wireOp",EDGE,"E103.4.3"),sQuery(id+"F8.wireOp",EDGE,"E103.5.0"),sQuery(id+"F8.wireOp",EDGE,"E103.5.1"),sQuery(id+"F8.wireOp",EDGE,"E103.5.2"),sQuery(id+"F8.wireOp",EDGE,"E103.5.3"),sQuery(id+"F8.wireOp",EDGE,"E103.6.0"),sQuery(id+"F8.wireOp",EDGE,"E103.6.1"),sQuery(id+"F8.wireOp",EDGE,"E103.6.2"),sQuery(id+"F8.wireOp",EDGE,"E103.6.3"),sQuery(id+"F8.wireOp",EDGE,"E103.7.0"),sQuery(id+"F8.wireOp",EDGE,"E103.7.1"),sQuery(id+"F8.wireOp",EDGE,"E103.7.2"),sQuery(id+"F8.wireOp",EDGE,"E103.7.3"),sQuery(id+"F8.wireOp",EDGE,"E105"),sQuery(id+"F8.wireOp",EDGE,"E106.1.0"),sQuery(id+"F8.wireOp",EDGE,"E106.1.1"),sQuery(id+"F8.wireOp",EDGE,"E106.1.2"),sQuery(id+"F8.wireOp",EDGE,"E106.1.3")])],"isStart":true});
            var sketch = newSketch(context, id + "F10", { "sketchPlane" : qUnion([Q0])});
            skArc(sketch, "E107", {"start": v(6.4, -8.83) * mm, "mid": v(-2.5, -10.6) * mm, "end": v(-9.67, -5.03) * mm});
            skArc(sketch, "E108", {"start": v(-5, -7.84) * mm, "mid": v(0, -9.3) * mm, "end": v(5, -7.84) * mm});
            skArc(sketch, "E109", {"start": v(6.6, -6.42) * mm, "mid": v(5.83, -7.12) * mm, "end": v(5, -7.72) * mm});
            skLineSegment(sketch, "E110", {"start": v(0, 0) * mm, "end": v(-9.67, 5.03) * mm, "construction": true});
            skLineSegment(sketch, "E111", {"start": v(-9.67, -5.03) * mm, "end": v(0, 0) * mm, "construction": true});
            skLineSegment(sketch, "E112", {"start": v(5, -7.84) * mm, "end": v(5, -7.72) * mm});
            skLineSegment(sketch, "E113", {"start": v(-5, -7.84) * mm, "end": v(-5, -7.72) * mm});
            skArc(sketch, "E114.trimOffspring", {"start": v(-5, -7.72) * mm, "mid": v(-5.83, -7.12) * mm, "end": v(-6.6, -6.42) * mm});
            skArc(sketch, "E115", {"start": v(-6.15, -3.75) * mm, "mid": v(0.86, -7.15) * mm, "end": v(6.86, -2.18) * mm, "construction": true});
            skLineSegment(sketch, "E116", {"start": v(-6.6, -6.42) * mm, "end": v(-5.54, -4.6) * mm});
            skLineSegment(sketch, "E117", {"start": v(6.6, -6.42) * mm, "end": v(5.54, -4.6) * mm});
            skArc(sketch, "E118", {"start": v(-5.54, -4.6) * mm, "mid": v(-5.68, -4.43) * mm, "end": v(-5.81, -4.25) * mm});
            skLineSegment(sketch, "E119", {"start": v(-5.81, -4.25) * mm, "end": v(-8.16, -4.25) * mm});
            skLineSegment(sketch, "E120", {"start": v(-8.16, -4.25) * mm, "end": v(-9.67, -5.03) * mm});
            skArc(sketch, "E121", {"start": v(5.54, -4.6) * mm, "mid": v(5.68, -4.43) * mm, "end": v(5.81, -4.25) * mm});
            skLineSegment(sketch, "E122", {"start": v(5.81, -4.25) * mm, "end": v(8.16, -4.25) * mm});
            skLineSegment(sketch, "E123", {"start": v(8.16, -4.25) * mm, "end": v(8.74, -4.55) * mm});
            skPoint(sketch, "E124.visualSharp", {"position": v(-9.67, 5.03) * mm});
            skArc(sketch, "E124.filletArc", {"start": v(9.11, -5.98) * mm, "mid": v(9.24, -5.18) * mm, "end": v(8.74, -4.55) * mm});
            skPoint(sketch, "E125.visualSharp", {"position": v(-9.67, -5.03) * mm});
            skLineSegment(sketch, "E126", {"start": v(5.26, -10.1) * mm, "end": v(5.59, -10.73) * mm});
            skLineSegment(sketch, "E127", {"start": v(5.59, -10.73) * mm, "end": v(5.76, -10.64) * mm});
            skPoint(sketch, "E128.newPointA", {"position": v(5.03, -9.67) * mm});
            skArc(sketch, "E128.filletArc", {"start": v(5.26, -10.1) * mm, "mid": v(4.98, -9.86) * mm, "end": v(4.6, -9.88) * mm});
            skArc(sketch, "E129", {"start": v(9.11, -5.98) * mm, "mid": v(7.88, -7.53) * mm, "end": v(6.4, -8.83) * mm});
            skArc(sketch, "E130.1.0", {"start": v(3.19, -10.93) * mm, "mid": v(2.96, -10.64) * mm, "end": v(2.59, -10.59) * mm});
            skLineSegment(sketch, "E130.1.1", {"start": v(3.19, -10.93) * mm, "end": v(3.39, -11.62) * mm});
            skLineSegment(sketch, "E130.1.2", {"start": v(3.39, -11.62) * mm, "end": v(3.58, -11.56) * mm});
            skLineSegment(sketch, "E130.1.3", {"start": v(4.6, -9.88) * mm, "end": v(3.58, -11.56) * mm});
            skArc(sketch, "E130.2.0", {"start": v(1, -11.35) * mm, "mid": v(0.82, -11.01) * mm, "end": v(0.47, -10.89) * mm});
            skLineSegment(sketch, "E130.2.1", {"start": v(1, -11.35) * mm, "end": v(1.05, -12.05) * mm});
            skLineSegment(sketch, "E130.2.2", {"start": v(1.05, -12.05) * mm, "end": v(1.25, -12.04) * mm});
            skLineSegment(sketch, "E130.2.3", {"start": v(2.59, -10.59) * mm, "end": v(1.25, -12.04) * mm});
            skArc(sketch, "E130.3.0", {"start": v(-1.24, -11.32) * mm, "mid": v(-1.34, -10.96) * mm, "end": v(-1.66, -10.77) * mm});
            skLineSegment(sketch, "E130.3.1", {"start": v(-1.24, -11.32) * mm, "end": v(-1.32, -12.03) * mm});
            skLineSegment(sketch, "E130.3.2", {"start": v(-1.32, -12.03) * mm, "end": v(-1.12, -12.05) * mm});
            skLineSegment(sketch, "E130.3.3", {"start": v(0.47, -10.89) * mm, "end": v(-1.12, -12.05) * mm});
            skArc(sketch, "E130.4.0", {"start": v(-3.42, -10.86) * mm, "mid": v(-3.45, -10.5) * mm, "end": v(-3.73, -10.24) * mm});
            skLineSegment(sketch, "E130.4.1", {"start": v(-3.42, -10.86) * mm, "end": v(-3.64, -11.54) * mm});
            skLineSegment(sketch, "E130.4.2", {"start": v(-3.64, -11.54) * mm, "end": v(-3.45, -11.6) * mm});
            skLineSegment(sketch, "E130.4.3", {"start": v(-1.66, -10.77) * mm, "end": v(-3.45, -11.6) * mm});
            skArc(sketch, "E130.5.0", {"start": v(-5.48, -9.99) * mm, "mid": v(-5.43, -9.62) * mm, "end": v(-5.66, -9.32) * mm});
            skLineSegment(sketch, "E130.5.1", {"start": v(-5.48, -9.99) * mm, "end": v(-5.82, -10.6) * mm});
            skLineSegment(sketch, "E130.5.2", {"start": v(-5.82, -10.6) * mm, "end": v(-5.64, -10.7) * mm});
            skLineSegment(sketch, "E130.5.3", {"start": v(-3.73, -10.24) * mm, "end": v(-5.64, -10.7) * mm});
            skArc(sketch, "E130.6.0", {"start": v(-7.32, -8.72) * mm, "mid": v(-7.2, -8.37) * mm, "end": v(-7.37, -8.03) * mm});
            skLineSegment(sketch, "E130.6.1", {"start": v(-7.32, -8.72) * mm, "end": v(-7.78, -9.27) * mm});
            skLineSegment(sketch, "E130.6.2", {"start": v(-7.78, -9.27) * mm, "end": v(-7.62, -9.4) * mm});
            skLineSegment(sketch, "E130.6.3", {"start": v(-5.66, -9.32) * mm, "end": v(-7.62, -9.4) * mm});
            skLineSegment(sketch, "E130.anchor1", {"start": v(0, 0) * mm, "end": v(4.82, -10.33) * mm, "construction": true});
            skLineSegment(sketch, "E130.anchor2", {"start": v(0, 0) * mm, "end": v(-10.33, -4.82) * mm, "construction": true});
            skLineSegment(sketch, "E131", {"start": v(6.4, -8.83) * mm, "end": v(7.19, -9.93) * mm, "construction": true});
            skLineSegment(sketch, "E132", {"start": v(5.76, -10.64) * mm, "end": v(6.4, -8.83) * mm});
            skArc(sketch, "E133.1.0", {"start": v(7.08, -8.92) * mm, "mid": v(6.75, -8.74) * mm, "end": v(6.4, -8.83) * mm});
            skLineSegment(sketch, "E133.1.1", {"start": v(7.08, -8.92) * mm, "end": v(7.52, -9.48) * mm});
            skLineSegment(sketch, "E133.1.2", {"start": v(7.52, -9.48) * mm, "end": v(7.68, -9.35) * mm});
            skLineSegment(sketch, "E133.1.3", {"start": v(7.68, -9.35) * mm, "end": v(7.95, -7.46) * mm});
            skPoint(sketch, "E133.center", {"position": v(0.04, -0.07) * mm});
            skLineSegment(sketch, "E133.anchor1", {"start": v(0.04, -0.07) * mm, "end": v(4.82, -10.33) * mm, "construction": true});
            skLineSegment(sketch, "E133.anchor2", {"start": v(0.04, -0.07) * mm, "end": v(6.69, -9.23) * mm, "construction": true});
            skSolve(sketch);
        }
        {
            var Q0;
            Q0 = qSketchRegion(id + "F10", true);
            extrude(context, id + "F11", {"entities" : qUnion([Q0]), "depth" : 0.5 * mm});
        }
        {
            var Q0;
            Q0=makeQuery(id+"F11.opExtrude","CAP_FACE",FACE,{"disambiguationData":[OSD([sQuery(id+"F10.wireOp",EDGE,"E107"),sQuery(id+"F10.wireOp",EDGE,"E108"),sQuery(id+"F10.wireOp",EDGE,"E109"),sQuery(id+"F10.wireOp",EDGE,"E112"),sQuery(id+"F10.wireOp",EDGE,"E113"),sQuery(id+"F10.wireOp",EDGE,"E114.trimOffspring"),sQuery(id+"F10.wireOp",EDGE,"E116"),sQuery(id+"F10.wireOp",EDGE,"E117"),sQuery(id+"F10.wireOp",EDGE,"E118"),sQuery(id+"F10.wireOp",EDGE,"E119"),sQuery(id+"F10.wireOp",EDGE,"E120"),sQuery(id+"F10.wireOp",EDGE,"E121"),sQuery(id+"F10.wireOp",EDGE,"E122"),sQuery(id+"F10.wireOp",EDGE,"E123"),sQuery(id+"F10.wireOp",EDGE,"E124.filletArc"),sQuery(id+"F10.wireOp",EDGE,"E126"),sQuery(id+"F10.wireOp",EDGE,"E127"),sQuery(id+"F10.wireOp",EDGE,"E128.filletArc"),sQuery(id+"F10.wireOp",EDGE,"E129"),sQuery(id+"F10.wireOp",EDGE,"E130.1.0"),sQuery(id+"F10.wireOp",EDGE,"E130.1.1"),sQuery(id+"F10.wireOp",EDGE,"E130.1.2"),sQuery(id+"F10.wireOp",EDGE,"E130.1.3"),sQuery(id+"F10.wireOp",EDGE,"E130.2.0"),sQuery(id+"F10.wireOp",EDGE,"E130.2.1"),sQuery(id+"F10.wireOp",EDGE,"E130.2.2"),sQuery(id+"F10.wireOp",EDGE,"E130.2.3"),sQuery(id+"F10.wireOp",EDGE,"E130.3.0"),sQuery(id+"F10.wireOp",EDGE,"E130.3.1"),sQuery(id+"F10.wireOp",EDGE,"E130.3.2"),sQuery(id+"F10.wireOp",EDGE,"E130.3.3"),sQuery(id+"F10.wireOp",EDGE,"E130.4.0"),sQuery(id+"F10.wireOp",EDGE,"E130.4.1"),sQuery(id+"F10.wireOp",EDGE,"E130.4.2"),sQuery(id+"F10.wireOp",EDGE,"E130.4.3"),sQuery(id+"F10.wireOp",EDGE,"E130.5.0"),sQuery(id+"F10.wireOp",EDGE,"E130.5.1"),sQuery(id+"F10.wireOp",EDGE,"E130.5.2"),sQuery(id+"F10.wireOp",EDGE,"E130.5.3"),sQuery(id+"F10.wireOp",EDGE,"E130.6.0"),sQuery(id+"F10.wireOp",EDGE,"E130.6.1"),sQuery(id+"F10.wireOp",EDGE,"E130.6.2"),sQuery(id+"F10.wireOp",EDGE,"E130.6.3"),sQuery(id+"F10.wireOp",EDGE,"E132"),sQuery(id+"F10.wireOp",EDGE,"E133.1.0"),sQuery(id+"F10.wireOp",EDGE,"E133.1.1"),sQuery(id+"F10.wireOp",EDGE,"E133.1.2"),sQuery(id+"F10.wireOp",EDGE,"E133.1.3")])],"isStart":false});
            var sketch = newSketch(context, id + "F12", { "sketchPlane" : qUnion([Q0])});
            skArc(sketch, "E134", {"start": v(9.11, -5.98) * mm, "mid": v(-0.55, -10.89) * mm, "end": v(-9.67, -5.03) * mm});
            skArc(sketch, "E135", {"start": v(-5, -7.84) * mm, "mid": v(0, -9.3) * mm, "end": v(5, -7.84) * mm});
            skArc(sketch, "E136", {"start": v(6.59, -6.42) * mm, "mid": v(5.83, -7.12) * mm, "end": v(5, -7.72) * mm});
            skLineSegment(sketch, "E137", {"start": v(9.97, -5.19) * mm, "end": v(0, 0) * mm, "construction": true});
            skLineSegment(sketch, "E138", {"start": v(-9.67, -5.03) * mm, "end": v(0, 0) * mm, "construction": true});
            skLineSegment(sketch, "E139", {"start": v(5, -7.84) * mm, "end": v(5, -7.72) * mm});
            skLineSegment(sketch, "E140", {"start": v(-5, -7.84) * mm, "end": v(-5, -7.72) * mm});
            skArc(sketch, "E141.trimOffspring", {"start": v(-5, -7.72) * mm, "mid": v(-5.83, -7.12) * mm, "end": v(-6.59, -6.42) * mm});
            skArc(sketch, "E142", {"start": v(-6.15, -3.75) * mm, "mid": v(0.86, -7.15) * mm, "end": v(6.86, -2.18) * mm, "construction": true});
            skLineSegment(sketch, "E143", {"start": v(-6.59, -6.42) * mm, "end": v(-5.54, -4.6) * mm});
            skLineSegment(sketch, "E144", {"start": v(6.59, -6.42) * mm, "end": v(5.54, -4.6) * mm});
            skArc(sketch, "E145", {"start": v(-5.54, -4.6) * mm, "mid": v(-5.68, -4.43) * mm, "end": v(-5.81, -4.25) * mm});
            skLineSegment(sketch, "E146", {"start": v(-5.81, -4.25) * mm, "end": v(-8.16, -4.25) * mm});
            skLineSegment(sketch, "E147", {"start": v(-8.16, -4.25) * mm, "end": v(-9.67, -5.03) * mm});
            skArc(sketch, "E148", {"start": v(5.54, -4.6) * mm, "mid": v(5.68, -4.43) * mm, "end": v(5.81, -4.25) * mm});
            skLineSegment(sketch, "E149", {"start": v(5.81, -4.25) * mm, "end": v(8.16, -4.25) * mm});
            skLineSegment(sketch, "E150", {"start": v(8.16, -4.25) * mm, "end": v(8.74, -4.55) * mm});
            skArc(sketch, "E151.filletArc", {"start": v(9.11, -5.98) * mm, "mid": v(9.24, -5.18) * mm, "end": v(8.74, -4.55) * mm});
            skPoint(sketch, "E152.visualSharp", {"position": v(-9.67, -5.03) * mm});
            skLineSegment(sketch, "E153", {"start": v(5.26, -10.1) * mm, "end": v(5.59, -10.73) * mm});
            skLineSegment(sketch, "E154", {"start": v(5.59, -10.73) * mm, "end": v(5.76, -10.64) * mm});
            skPoint(sketch, "E155.newPointA", {"position": v(5.03, -9.67) * mm});
            skArc(sketch, "E155.filletArc", {"start": v(5.26, -10.1) * mm, "mid": v(4.98, -9.86) * mm, "end": v(4.6, -9.88) * mm});
            skArc(sketch, "E156.1.0", {"start": v(3.19, -10.93) * mm, "mid": v(2.96, -10.64) * mm, "end": v(2.59, -10.59) * mm});
            skLineSegment(sketch, "E156.1.1", {"start": v(3.19, -10.93) * mm, "end": v(3.39, -11.62) * mm});
            skLineSegment(sketch, "E156.1.2", {"start": v(3.39, -11.62) * mm, "end": v(3.58, -11.56) * mm});
            skLineSegment(sketch, "E156.1.3", {"start": v(4.6, -9.88) * mm, "end": v(3.58, -11.56) * mm});
            skArc(sketch, "E156.2.0", {"start": v(1, -11.35) * mm, "mid": v(0.82, -11.01) * mm, "end": v(0.47, -10.89) * mm});
            skLineSegment(sketch, "E156.2.1", {"start": v(1, -11.35) * mm, "end": v(1.05, -12.05) * mm});
            skLineSegment(sketch, "E156.2.2", {"start": v(1.05, -12.05) * mm, "end": v(1.25, -12.04) * mm});
            skLineSegment(sketch, "E156.2.3", {"start": v(2.59, -10.59) * mm, "end": v(1.25, -12.04) * mm});
            skArc(sketch, "E156.3.0", {"start": v(-1.24, -11.32) * mm, "mid": v(-1.34, -10.96) * mm, "end": v(-1.66, -10.77) * mm});
            skLineSegment(sketch, "E156.3.1", {"start": v(-1.24, -11.32) * mm, "end": v(-1.32, -12.03) * mm});
            skLineSegment(sketch, "E156.3.2", {"start": v(-1.32, -12.03) * mm, "end": v(-1.12, -12.05) * mm});
            skLineSegment(sketch, "E156.3.3", {"start": v(0.47, -10.89) * mm, "end": v(-1.12, -12.05) * mm});
            skArc(sketch, "E156.4.0", {"start": v(-3.42, -10.86) * mm, "mid": v(-3.45, -10.5) * mm, "end": v(-3.73, -10.24) * mm});
            skLineSegment(sketch, "E156.4.1", {"start": v(-3.42, -10.86) * mm, "end": v(-3.64, -11.54) * mm});
            skLineSegment(sketch, "E156.4.2", {"start": v(-3.64, -11.54) * mm, "end": v(-3.45, -11.6) * mm});
            skLineSegment(sketch, "E156.4.3", {"start": v(-1.66, -10.77) * mm, "end": v(-3.45, -11.6) * mm});
            skArc(sketch, "E156.5.0", {"start": v(-5.48, -9.99) * mm, "mid": v(-5.43, -9.62) * mm, "end": v(-5.66, -9.32) * mm});
            skLineSegment(sketch, "E156.5.1", {"start": v(-5.48, -9.99) * mm, "end": v(-5.82, -10.6) * mm});
            skLineSegment(sketch, "E156.5.2", {"start": v(-5.82, -10.6) * mm, "end": v(-5.64, -10.7) * mm});
            skLineSegment(sketch, "E156.5.3", {"start": v(-3.73, -10.24) * mm, "end": v(-5.64, -10.7) * mm});
            skLineSegment(sketch, "E156.anchor1", {"start": v(0, 0) * mm, "end": v(4.82, -10.33) * mm, "construction": true});
            skLineSegment(sketch, "E156.anchor2", {"start": v(0, 0) * mm, "end": v(-10.33, -4.82) * mm, "construction": true});
            skLineSegment(sketch, "E157", {"start": v(6.4, -8.82) * mm, "end": v(7.2, -9.94) * mm, "construction": true});
            skLineSegment(sketch, "E158", {"start": v(5.76, -10.64) * mm, "end": v(6.4, -8.82) * mm});
            skArc(sketch, "E159.1.0", {"start": v(7.09, -8.91) * mm, "mid": v(6.77, -8.73) * mm, "end": v(6.4, -8.82) * mm});
            skLineSegment(sketch, "E159.1.1", {"start": v(7.09, -8.91) * mm, "end": v(7.53, -9.47) * mm});
            skLineSegment(sketch, "E159.1.2", {"start": v(7.53, -9.47) * mm, "end": v(7.69, -9.35) * mm});
            skLineSegment(sketch, "E159.1.3", {"start": v(7.69, -9.35) * mm, "end": v(7.97, -7.44) * mm});
            skLineSegment(sketch, "E159.anchor2", {"start": v(0, 0) * mm, "end": v(6.7, -9.22) * mm, "construction": true});
            skSolve(sketch);
        }
        {
            var Q0;
            Q0 = qSketchRegion(id + "F12", true);
            extrude(context, id + "F13", {"entities" : qUnion([Q0]), "depth" : 0.5 * mm});
        }
        {
            var Q0;
            Q0=makeQuery(id+"F13.opExtrude","CAP_FACE",FACE,{"disambiguationData":[OSD([sQuery(id+"F12.wireOp",EDGE,"E134"),sQuery(id+"F12.wireOp",EDGE,"E135"),sQuery(id+"F12.wireOp",EDGE,"E136"),sQuery(id+"F12.wireOp",EDGE,"E139"),sQuery(id+"F12.wireOp",EDGE,"E140"),sQuery(id+"F12.wireOp",EDGE,"E141.trimOffspring"),sQuery(id+"F12.wireOp",EDGE,"E143"),sQuery(id+"F12.wireOp",EDGE,"E144"),sQuery(id+"F12.wireOp",EDGE,"E145"),sQuery(id+"F12.wireOp",EDGE,"E146"),sQuery(id+"F12.wireOp",EDGE,"E147"),sQuery(id+"F12.wireOp",EDGE,"E148"),sQuery(id+"F12.wireOp",EDGE,"E149"),sQuery(id+"F12.wireOp",EDGE,"E150"),sQuery(id+"F12.wireOp",EDGE,"E151.filletArc"),sQuery(id+"F12.wireOp",EDGE,"E153"),sQuery(id+"F12.wireOp",EDGE,"E154"),sQuery(id+"F12.wireOp",EDGE,"E155.filletArc"),sQuery(id+"F12.wireOp",EDGE,"E156.1.0"),sQuery(id+"F12.wireOp",EDGE,"E156.1.1"),sQuery(id+"F12.wireOp",EDGE,"E156.1.2"),sQuery(id+"F12.wireOp",EDGE,"E156.1.3"),sQuery(id+"F12.wireOp",EDGE,"E156.2.0"),sQuery(id+"F12.wireOp",EDGE,"E156.2.1"),sQuery(id+"F12.wireOp",EDGE,"E156.2.2"),sQuery(id+"F12.wireOp",EDGE,"E156.2.3"),sQuery(id+"F12.wireOp",EDGE,"E156.3.0"),sQuery(id+"F12.wireOp",EDGE,"E156.3.1"),sQuery(id+"F12.wireOp",EDGE,"E156.3.2"),sQuery(id+"F12.wireOp",EDGE,"E156.3.3"),sQuery(id+"F12.wireOp",EDGE,"E156.4.0"),sQuery(id+"F12.wireOp",EDGE,"E156.4.1"),sQuery(id+"F12.wireOp",EDGE,"E156.4.2"),sQuery(id+"F12.wireOp",EDGE,"E156.4.3"),sQuery(id+"F12.wireOp",EDGE,"E156.5.0"),sQuery(id+"F12.wireOp",EDGE,"E156.5.1"),sQuery(id+"F12.wireOp",EDGE,"E156.5.2"),sQuery(id+"F12.wireOp",EDGE,"E156.5.3"),sQuery(id+"F12.wireOp",EDGE,"E158"),sQuery(id+"F12.wireOp",EDGE,"E159.1.0"),sQuery(id+"F12.wireOp",EDGE,"E159.1.1"),sQuery(id+"F12.wireOp",EDGE,"E159.1.2"),sQuery(id+"F12.wireOp",EDGE,"E159.1.3")])],"isStart":false});
            var sketch = newSketch(context, id + "F14", { "sketchPlane" : qUnion([Q0])});
            skArc(sketch, "E160", {"start": v(9.11, -5.98) * mm, "mid": v(-0.55, -10.89) * mm, "end": v(-9.67, -5.03) * mm});
            skArc(sketch, "E161", {"start": v(-5, -7.84) * mm, "mid": v(0, -9.3) * mm, "end": v(5, -7.84) * mm});
            skArc(sketch, "E162", {"start": v(6.59, -6.42) * mm, "mid": v(5.83, -7.12) * mm, "end": v(5, -7.72) * mm});
            skLineSegment(sketch, "E163", {"start": v(9.97, -5.19) * mm, "end": v(0, 0) * mm, "construction": true});
            skLineSegment(sketch, "E164", {"start": v(-9.67, -5.03) * mm, "end": v(0, 0) * mm, "construction": true});
            skLineSegment(sketch, "E165", {"start": v(5, -7.84) * mm, "end": v(5, -7.72) * mm});
            skLineSegment(sketch, "E166", {"start": v(-5, -7.84) * mm, "end": v(-5, -7.72) * mm});
            skArc(sketch, "E167.trimOffspring", {"start": v(-5, -7.72) * mm, "mid": v(-5.83, -7.12) * mm, "end": v(-6.59, -6.42) * mm});
            skArc(sketch, "E168", {"start": v(-6.15, -3.75) * mm, "mid": v(0.86, -7.15) * mm, "end": v(6.86, -2.18) * mm, "construction": true});
            skLineSegment(sketch, "E169", {"start": v(-6.59, -6.42) * mm, "end": v(-5.54, -4.6) * mm});
            skLineSegment(sketch, "E170", {"start": v(6.59, -6.42) * mm, "end": v(5.54, -4.6) * mm});
            skArc(sketch, "E171", {"start": v(-5.54, -4.6) * mm, "mid": v(-5.68, -4.43) * mm, "end": v(-5.81, -4.25) * mm});
            skLineSegment(sketch, "E172", {"start": v(-5.81, -4.25) * mm, "end": v(-8.16, -4.25) * mm});
            skLineSegment(sketch, "E173", {"start": v(-8.16, -4.25) * mm, "end": v(-9.67, -5.03) * mm});
            skArc(sketch, "E174", {"start": v(5.54, -4.6) * mm, "mid": v(5.68, -4.43) * mm, "end": v(5.81, -4.25) * mm});
            skLineSegment(sketch, "E175", {"start": v(5.81, -4.25) * mm, "end": v(8.16, -4.25) * mm});
            skLineSegment(sketch, "E176", {"start": v(8.16, -4.25) * mm, "end": v(8.74, -4.55) * mm});
            skArc(sketch, "E177.filletArc", {"start": v(9.11, -5.98) * mm, "mid": v(9.24, -5.18) * mm, "end": v(8.74, -4.55) * mm});
            skPoint(sketch, "E178.visualSharp", {"position": v(-9.67, -5.03) * mm});
            skLineSegment(sketch, "E179", {"start": v(5.26, -10.1) * mm, "end": v(5.59, -10.73) * mm});
            skLineSegment(sketch, "E180", {"start": v(5.59, -10.73) * mm, "end": v(5.76, -10.64) * mm});
            skPoint(sketch, "E181.newPointA", {"position": v(5.03, -9.67) * mm});
            skArc(sketch, "E181.filletArc", {"start": v(5.26, -10.1) * mm, "mid": v(4.98, -9.86) * mm, "end": v(4.6, -9.88) * mm});
            skArc(sketch, "E182.1.0", {"start": v(3.19, -10.93) * mm, "mid": v(2.96, -10.64) * mm, "end": v(2.59, -10.59) * mm});
            skLineSegment(sketch, "E182.1.1", {"start": v(3.19, -10.93) * mm, "end": v(3.39, -11.62) * mm});
            skLineSegment(sketch, "E182.1.2", {"start": v(3.39, -11.62) * mm, "end": v(3.58, -11.56) * mm});
            skLineSegment(sketch, "E182.1.3", {"start": v(4.6, -9.88) * mm, "end": v(3.58, -11.56) * mm});
            skArc(sketch, "E182.2.0", {"start": v(1, -11.35) * mm, "mid": v(0.82, -11.01) * mm, "end": v(0.47, -10.89) * mm});
            skLineSegment(sketch, "E182.2.1", {"start": v(1, -11.35) * mm, "end": v(1.05, -12.05) * mm});
            skLineSegment(sketch, "E182.2.2", {"start": v(1.05, -12.05) * mm, "end": v(1.25, -12.04) * mm});
            skLineSegment(sketch, "E182.2.3", {"start": v(2.59, -10.59) * mm, "end": v(1.25, -12.04) * mm});
            skArc(sketch, "E182.3.0", {"start": v(-1.24, -11.32) * mm, "mid": v(-1.34, -10.96) * mm, "end": v(-1.66, -10.77) * mm});
            skLineSegment(sketch, "E182.3.1", {"start": v(-1.24, -11.32) * mm, "end": v(-1.32, -12.03) * mm});
            skLineSegment(sketch, "E182.3.2", {"start": v(-1.32, -12.03) * mm, "end": v(-1.12, -12.05) * mm});
            skLineSegment(sketch, "E182.3.3", {"start": v(0.47, -10.89) * mm, "end": v(-1.12, -12.05) * mm});
            skArc(sketch, "E182.4.0", {"start": v(-3.42, -10.86) * mm, "mid": v(-3.45, -10.5) * mm, "end": v(-3.73, -10.24) * mm});
            skLineSegment(sketch, "E182.4.1", {"start": v(-3.42, -10.86) * mm, "end": v(-3.64, -11.54) * mm});
            skLineSegment(sketch, "E182.4.2", {"start": v(-3.64, -11.54) * mm, "end": v(-3.45, -11.6) * mm});
            skLineSegment(sketch, "E182.4.3", {"start": v(-1.66, -10.77) * mm, "end": v(-3.45, -11.6) * mm});
            skLineSegment(sketch, "E182.anchor1", {"start": v(0, 0) * mm, "end": v(4.82, -10.33) * mm, "construction": true});
            skLineSegment(sketch, "E182.anchor2", {"start": v(0, 0) * mm, "end": v(-10.33, -4.82) * mm, "construction": true});
            skLineSegment(sketch, "E183", {"start": v(6.4, -8.82) * mm, "end": v(7.2, -9.94) * mm, "construction": true});
            skLineSegment(sketch, "E184", {"start": v(5.76, -10.64) * mm, "end": v(6.4, -8.82) * mm});
            skArc(sketch, "E185.1.0", {"start": v(7.09, -8.91) * mm, "mid": v(6.77, -8.73) * mm, "end": v(6.4, -8.82) * mm});
            skLineSegment(sketch, "E185.1.1", {"start": v(7.09, -8.91) * mm, "end": v(7.53, -9.47) * mm});
            skLineSegment(sketch, "E185.1.2", {"start": v(7.53, -9.47) * mm, "end": v(7.69, -9.35) * mm});
            skLineSegment(sketch, "E185.1.3", {"start": v(7.69, -9.35) * mm, "end": v(7.97, -7.44) * mm});
            skLineSegment(sketch, "E185.anchor2", {"start": v(0, 0) * mm, "end": v(6.7, -9.22) * mm, "construction": true});
            skSolve(sketch);
        }
        {
            var Q0;
            {var subQ2=sQuery(id+"F14.wireOp",EDGE,"E185.1.0");Q0=makeQuery(id+"F14.imprint","IMPRINT",FACE,{"disambiguationData":[TD([[makeQuery(id+"F14.imprint","IMPRINT",EDGE,{"derivedFrom":subQ2}),-1.0]])]});}
            var Q1;
            Q1=makeQuery(id+"F14.imprint","IMPRINT",FACE,{"disambiguationData":[TD([[makeQuery(id+"F14.imprint","IMPRINT",EDGE,{"derivedFrom":sQuery(id+"F14.wireOp",EDGE,"E179")}),1.0]])]});
            var Q2;
            {var subQ1=sQuery(id+"F14.wireOp",EDGE,"E182.1.0");Q2=makeQuery(id+"F14.imprint","IMPRINT",FACE,{"disambiguationData":[TD([[makeQuery(id+"F14.imprint","IMPRINT",EDGE,{"derivedFrom":subQ1}),-1.0]])]});}
            var Q3;
            {var subQ2=sQuery(id+"F14.wireOp",EDGE,"E182.2.0");Q3=makeQuery(id+"F14.imprint","IMPRINT",FACE,{"disambiguationData":[TD([[makeQuery(id+"F14.imprint","IMPRINT",EDGE,{"derivedFrom":subQ2}),-1.0]])]});}
            var Q4;
            {var subQ2=sQuery(id+"F14.wireOp",EDGE,"E182.3.0");Q4=makeQuery(id+"F14.imprint","IMPRINT",FACE,{"disambiguationData":[TD([[makeQuery(id+"F14.imprint","IMPRINT",EDGE,{"derivedFrom":subQ2}),-1.0]])]});}
            var Q5;
            {var subQ2=sQuery(id+"F14.wireOp",EDGE,"E182.4.0");Q5=makeQuery(id+"F14.imprint","IMPRINT",FACE,{"disambiguationData":[TD([[makeQuery(id+"F14.imprint","IMPRINT",EDGE,{"derivedFrom":subQ2}),-1.0]])]});}
            var Q6;
            Q6=makeQuery(id+"F14.imprint","IMPRINT",FACE,{"disambiguationData":[TD([[makeQuery(id+"F14.imprint","IMPRINT",EDGE,{"derivedFrom":sQuery(id+"F14.wireOp",EDGE,"E161")}),-1.0]])]});
            extrude(context, id + "F15", {"entities" : qUnion([Q0, Q1, Q2, Q3, Q4, Q5, Q6]), "depth" : 0.5 * mm});
        }
        {
            var Q0;
            Q0=makeQuery(id+"F15.opExtrude","CAP_FACE",FACE,{"disambiguationData":[OSD([sQuery(id+"F14.wireOp",EDGE,"E160"),sQuery(id+"F14.wireOp",EDGE,"E161"),sQuery(id+"F14.wireOp",EDGE,"E162"),sQuery(id+"F14.wireOp",EDGE,"E165"),sQuery(id+"F14.wireOp",EDGE,"E166"),sQuery(id+"F14.wireOp",EDGE,"E167.trimOffspring"),sQuery(id+"F14.wireOp",EDGE,"E169"),sQuery(id+"F14.wireOp",EDGE,"E170"),sQuery(id+"F14.wireOp",EDGE,"E171"),sQuery(id+"F14.wireOp",EDGE,"E172"),sQuery(id+"F14.wireOp",EDGE,"E173"),sQuery(id+"F14.wireOp",EDGE,"E174"),sQuery(id+"F14.wireOp",EDGE,"E175"),sQuery(id+"F14.wireOp",EDGE,"E176"),sQuery(id+"F14.wireOp",EDGE,"E177.filletArc"),sQuery(id+"F14.wireOp",EDGE,"E179"),sQuery(id+"F14.wireOp",EDGE,"E180"),sQuery(id+"F14.wireOp",EDGE,"E181.filletArc"),sQuery(id+"F14.wireOp",EDGE,"E182.1.0"),sQuery(id+"F14.wireOp",EDGE,"E182.1.1"),sQuery(id+"F14.wireOp",EDGE,"E182.1.2"),sQuery(id+"F14.wireOp",EDGE,"E182.1.3"),sQuery(id+"F14.wireOp",EDGE,"E182.2.0"),sQuery(id+"F14.wireOp",EDGE,"E182.2.1"),sQuery(id+"F14.wireOp",EDGE,"E182.2.2"),sQuery(id+"F14.wireOp",EDGE,"E182.2.3"),sQuery(id+"F14.wireOp",EDGE,"E182.3.0"),sQuery(id+"F14.wireOp",EDGE,"E182.3.1"),sQuery(id+"F14.wireOp",EDGE,"E182.3.2"),sQuery(id+"F14.wireOp",EDGE,"E182.3.3"),sQuery(id+"F14.wireOp",EDGE,"E182.4.0"),sQuery(id+"F14.wireOp",EDGE,"E182.4.1"),sQuery(id+"F14.wireOp",EDGE,"E182.4.2"),sQuery(id+"F14.wireOp",EDGE,"E182.4.3"),sQuery(id+"F14.wireOp",EDGE,"E184"),sQuery(id+"F14.wireOp",EDGE,"E185.1.0"),sQuery(id+"F14.wireOp",EDGE,"E185.1.1"),sQuery(id+"F14.wireOp",EDGE,"E185.1.2"),sQuery(id+"F14.wireOp",EDGE,"E185.1.3")])],"isStart":false});
            var sketch = newSketch(context, id + "F16", { "sketchPlane" : qUnion([Q0])});
            skArc(sketch, "E186", {"start": v(9.11, -5.98) * mm, "mid": v(-0.55, -10.89) * mm, "end": v(-9.67, -5.03) * mm});
            skArc(sketch, "E187", {"start": v(-5, -7.84) * mm, "mid": v(0, -9.3) * mm, "end": v(5, -7.84) * mm});
            skArc(sketch, "E188", {"start": v(6.59, -6.42) * mm, "mid": v(5.83, -7.12) * mm, "end": v(5, -7.72) * mm});
            skLineSegment(sketch, "E189", {"start": v(9.97, -5.19) * mm, "end": v(0, 0) * mm, "construction": true});
            skLineSegment(sketch, "E190", {"start": v(-9.67, -5.03) * mm, "end": v(0, 0) * mm, "construction": true});
            skLineSegment(sketch, "E191", {"start": v(5, -7.84) * mm, "end": v(5, -7.72) * mm});
            skLineSegment(sketch, "E192", {"start": v(-5, -7.84) * mm, "end": v(-5, -7.72) * mm});
            skArc(sketch, "E193.trimOffspring", {"start": v(-5, -7.72) * mm, "mid": v(-5.83, -7.12) * mm, "end": v(-6.59, -6.42) * mm});
            skArc(sketch, "E194", {"start": v(-6.15, -3.75) * mm, "mid": v(0.86, -7.15) * mm, "end": v(6.86, -2.18) * mm, "construction": true});
            skLineSegment(sketch, "E195", {"start": v(-6.59, -6.42) * mm, "end": v(-5.54, -4.6) * mm});
            skLineSegment(sketch, "E196", {"start": v(6.59, -6.42) * mm, "end": v(5.54, -4.6) * mm});
            skArc(sketch, "E197", {"start": v(-5.54, -4.6) * mm, "mid": v(-5.68, -4.43) * mm, "end": v(-5.81, -4.25) * mm});
            skLineSegment(sketch, "E198", {"start": v(-5.81, -4.25) * mm, "end": v(-8.16, -4.25) * mm});
            skLineSegment(sketch, "E199", {"start": v(-8.16, -4.25) * mm, "end": v(-9.67, -5.03) * mm});
            skArc(sketch, "E200", {"start": v(5.54, -4.6) * mm, "mid": v(5.68, -4.43) * mm, "end": v(5.81, -4.25) * mm});
            skLineSegment(sketch, "E201", {"start": v(5.81, -4.25) * mm, "end": v(8.16, -4.25) * mm});
            skLineSegment(sketch, "E202", {"start": v(8.16, -4.25) * mm, "end": v(8.74, -4.55) * mm});
            skArc(sketch, "E203.filletArc", {"start": v(9.11, -5.98) * mm, "mid": v(9.24, -5.18) * mm, "end": v(8.74, -4.55) * mm});
            skPoint(sketch, "E204.visualSharp", {"position": v(-9.67, -5.03) * mm});
            skLineSegment(sketch, "E205", {"start": v(5.26, -10.1) * mm, "end": v(5.59, -10.73) * mm});
            skLineSegment(sketch, "E206", {"start": v(5.59, -10.73) * mm, "end": v(5.76, -10.64) * mm});
            skPoint(sketch, "E207.newPointA", {"position": v(5.03, -9.67) * mm});
            skArc(sketch, "E207.filletArc", {"start": v(5.26, -10.1) * mm, "mid": v(4.98, -9.86) * mm, "end": v(4.6, -9.88) * mm});
            skArc(sketch, "E208.1.0", {"start": v(3.19, -10.93) * mm, "mid": v(2.96, -10.64) * mm, "end": v(2.59, -10.59) * mm});
            skLineSegment(sketch, "E208.1.1", {"start": v(3.19, -10.93) * mm, "end": v(3.39, -11.62) * mm});
            skLineSegment(sketch, "E208.1.2", {"start": v(3.39, -11.62) * mm, "end": v(3.58, -11.56) * mm});
            skLineSegment(sketch, "E208.1.3", {"start": v(4.6, -9.88) * mm, "end": v(3.58, -11.56) * mm});
            skArc(sketch, "E208.2.0", {"start": v(1, -11.35) * mm, "mid": v(0.82, -11.01) * mm, "end": v(0.47, -10.89) * mm});
            skLineSegment(sketch, "E208.2.1", {"start": v(1, -11.35) * mm, "end": v(1.05, -12.05) * mm});
            skLineSegment(sketch, "E208.2.2", {"start": v(1.05, -12.05) * mm, "end": v(1.25, -12.04) * mm});
            skLineSegment(sketch, "E208.2.3", {"start": v(2.59, -10.59) * mm, "end": v(1.25, -12.04) * mm});
            skArc(sketch, "E208.3.0", {"start": v(-1.24, -11.32) * mm, "mid": v(-1.34, -10.96) * mm, "end": v(-1.66, -10.77) * mm});
            skLineSegment(sketch, "E208.3.1", {"start": v(-1.24, -11.32) * mm, "end": v(-1.32, -12.03) * mm});
            skLineSegment(sketch, "E208.3.2", {"start": v(-1.32, -12.03) * mm, "end": v(-1.12, -12.05) * mm});
            skLineSegment(sketch, "E208.3.3", {"start": v(0.47, -10.89) * mm, "end": v(-1.12, -12.05) * mm});
            skLineSegment(sketch, "E208.anchor1", {"start": v(0, 0) * mm, "end": v(4.82, -10.33) * mm, "construction": true});
            skLineSegment(sketch, "E208.anchor2", {"start": v(0, 0) * mm, "end": v(-10.33, -4.82) * mm, "construction": true});
            skLineSegment(sketch, "E209", {"start": v(6.4, -8.82) * mm, "end": v(7.2, -9.94) * mm, "construction": true});
            skLineSegment(sketch, "E210", {"start": v(5.76, -10.64) * mm, "end": v(6.4, -8.82) * mm});
            skArc(sketch, "E211.1.0", {"start": v(7.09, -8.91) * mm, "mid": v(6.77, -8.73) * mm, "end": v(6.4, -8.82) * mm});
            skLineSegment(sketch, "E211.1.1", {"start": v(7.09, -8.91) * mm, "end": v(7.53, -9.47) * mm});
            skLineSegment(sketch, "E211.1.2", {"start": v(7.53, -9.47) * mm, "end": v(7.69, -9.35) * mm});
            skLineSegment(sketch, "E211.1.3", {"start": v(7.69, -9.35) * mm, "end": v(7.97, -7.44) * mm});
            skLineSegment(sketch, "E211.anchor2", {"start": v(0, 0) * mm, "end": v(6.7, -9.22) * mm, "construction": true});
            skSolve(sketch);
        }
        {
            var Q0;
            {var subQ2=sQuery(id+"F16.wireOp",EDGE,"E211.1.0");Q0=makeQuery(id+"F16.imprint","IMPRINT",FACE,{"disambiguationData":[TD([[makeQuery(id+"F16.imprint","IMPRINT",EDGE,{"derivedFrom":subQ2}),-1.0]])]});}
            var Q1;
            Q1=makeQuery(id+"F16.imprint","IMPRINT",FACE,{"disambiguationData":[TD([[makeQuery(id+"F16.imprint","IMPRINT",EDGE,{"derivedFrom":sQuery(id+"F16.wireOp",EDGE,"E205")}),1.0]])]});
            var Q2;
            {var subQ2=sQuery(id+"F16.wireOp",EDGE,"E208.1.0");Q2=makeQuery(id+"F16.imprint","IMPRINT",FACE,{"disambiguationData":[TD([[makeQuery(id+"F16.imprint","IMPRINT",EDGE,{"derivedFrom":subQ2}),-1.0]])]});}
            var Q3;
            {var subQ1=sQuery(id+"F16.wireOp",EDGE,"E208.2.0");Q3=makeQuery(id+"F16.imprint","IMPRINT",FACE,{"disambiguationData":[TD([[makeQuery(id+"F16.imprint","IMPRINT",EDGE,{"derivedFrom":subQ1}),-1.0]])]});}
            var Q4;
            {var subQ2=sQuery(id+"F16.wireOp",EDGE,"E208.3.0");Q4=makeQuery(id+"F16.imprint","IMPRINT",FACE,{"disambiguationData":[TD([[makeQuery(id+"F16.imprint","IMPRINT",EDGE,{"derivedFrom":subQ2}),-1.0]])]});}
            var Q5;
            Q5=makeQuery(id+"F16.imprint","IMPRINT",FACE,{"disambiguationData":[TD([[makeQuery(id+"F16.imprint","IMPRINT",EDGE,{"derivedFrom":sQuery(id+"F16.wireOp",EDGE,"E187")}),-1.0]])]});
            extrude(context, id + "F17", {"entities" : qUnion([Q0, Q1, Q2, Q3, Q4, Q5]), "depth" : 2.5 * mm});
        }
        {
            var Q0;
            Q0=makeQuery(id+"F17.opExtrude","CAP_FACE",FACE,{"disambiguationData":[OSD([sQuery(id+"F16.wireOp",EDGE,"E186"),sQuery(id+"F16.wireOp",EDGE,"E187"),sQuery(id+"F16.wireOp",EDGE,"E188"),sQuery(id+"F16.wireOp",EDGE,"E191"),sQuery(id+"F16.wireOp",EDGE,"E192"),sQuery(id+"F16.wireOp",EDGE,"E193.trimOffspring"),sQuery(id+"F16.wireOp",EDGE,"E195"),sQuery(id+"F16.wireOp",EDGE,"E196"),sQuery(id+"F16.wireOp",EDGE,"E197"),sQuery(id+"F16.wireOp",EDGE,"E198"),sQuery(id+"F16.wireOp",EDGE,"E199"),sQuery(id+"F16.wireOp",EDGE,"E200"),sQuery(id+"F16.wireOp",EDGE,"E201"),sQuery(id+"F16.wireOp",EDGE,"E202"),sQuery(id+"F16.wireOp",EDGE,"E203.filletArc"),sQuery(id+"F16.wireOp",EDGE,"E205"),sQuery(id+"F16.wireOp",EDGE,"E206"),sQuery(id+"F16.wireOp",EDGE,"E207.filletArc"),sQuery(id+"F16.wireOp",EDGE,"E208.1.0"),sQuery(id+"F16.wireOp",EDGE,"E208.1.1"),sQuery(id+"F16.wireOp",EDGE,"E208.1.2"),sQuery(id+"F16.wireOp",EDGE,"E208.1.3"),sQuery(id+"F16.wireOp",EDGE,"E208.2.0"),sQuery(id+"F16.wireOp",EDGE,"E208.2.1"),sQuery(id+"F16.wireOp",EDGE,"E208.2.2"),sQuery(id+"F16.wireOp",EDGE,"E208.2.3"),sQuery(id+"F16.wireOp",EDGE,"E208.3.0"),sQuery(id+"F16.wireOp",EDGE,"E208.3.1"),sQuery(id+"F16.wireOp",EDGE,"E208.3.2"),sQuery(id+"F16.wireOp",EDGE,"E208.3.3"),sQuery(id+"F16.wireOp",EDGE,"E210"),sQuery(id+"F16.wireOp",EDGE,"E211.1.0"),sQuery(id+"F16.wireOp",EDGE,"E211.1.1"),sQuery(id+"F16.wireOp",EDGE,"E211.1.2"),sQuery(id+"F16.wireOp",EDGE,"E211.1.3")])],"isStart":false});
            var sketch = newSketch(context, id + "F18", { "sketchPlane" : qUnion([Q0])});
            skArc(sketch, "E212", {"start": v(9.11, -5.98) * mm, "mid": v(-0.55, -10.89) * mm, "end": v(-9.67, -5.03) * mm});
            skArc(sketch, "E213", {"start": v(-5, -7.84) * mm, "mid": v(0, -9.3) * mm, "end": v(5, -7.84) * mm});
            skArc(sketch, "E214", {"start": v(6.59, -6.42) * mm, "mid": v(5.83, -7.12) * mm, "end": v(5, -7.72) * mm});
            skLineSegment(sketch, "E215", {"start": v(9.97, -5.19) * mm, "end": v(0, 0) * mm, "construction": true});
            skLineSegment(sketch, "E216", {"start": v(-9.67, -5.03) * mm, "end": v(0, 0) * mm, "construction": true});
            skLineSegment(sketch, "E217", {"start": v(5, -7.84) * mm, "end": v(5, -7.72) * mm});
            skLineSegment(sketch, "E218", {"start": v(-5, -7.84) * mm, "end": v(-5, -7.72) * mm});
            skArc(sketch, "E219.trimOffspring", {"start": v(-5, -7.72) * mm, "mid": v(-5.83, -7.12) * mm, "end": v(-6.59, -6.42) * mm});
            skArc(sketch, "E220", {"start": v(-6.15, -3.75) * mm, "mid": v(0.86, -7.15) * mm, "end": v(6.86, -2.18) * mm, "construction": true});
            skLineSegment(sketch, "E221", {"start": v(-6.59, -6.42) * mm, "end": v(-5.54, -4.6) * mm});
            skLineSegment(sketch, "E222", {"start": v(6.59, -6.42) * mm, "end": v(5.54, -4.6) * mm});
            skArc(sketch, "E223", {"start": v(-5.54, -4.6) * mm, "mid": v(-5.68, -4.43) * mm, "end": v(-5.81, -4.25) * mm});
            skLineSegment(sketch, "E224", {"start": v(-5.81, -4.25) * mm, "end": v(-8.16, -4.25) * mm});
            skLineSegment(sketch, "E225", {"start": v(-8.16, -4.25) * mm, "end": v(-9.67, -5.03) * mm});
            skArc(sketch, "E226", {"start": v(5.54, -4.6) * mm, "mid": v(5.68, -4.43) * mm, "end": v(5.81, -4.25) * mm});
            skLineSegment(sketch, "E227", {"start": v(5.81, -4.25) * mm, "end": v(8.16, -4.25) * mm});
            skLineSegment(sketch, "E228", {"start": v(8.16, -4.25) * mm, "end": v(8.74, -4.55) * mm});
            skArc(sketch, "E229.filletArc", {"start": v(9.11, -5.98) * mm, "mid": v(9.24, -5.18) * mm, "end": v(8.74, -4.55) * mm});
            skPoint(sketch, "E230.visualSharp", {"position": v(-9.67, -5.03) * mm});
            skLineSegment(sketch, "E231", {"start": v(5.26, -10.1) * mm, "end": v(5.59, -10.73) * mm});
            skLineSegment(sketch, "E232", {"start": v(5.59, -10.73) * mm, "end": v(5.76, -10.64) * mm});
            skPoint(sketch, "E233.newPointA", {"position": v(5.03, -9.67) * mm});
            skArc(sketch, "E233.filletArc", {"start": v(5.26, -10.1) * mm, "mid": v(4.98, -9.86) * mm, "end": v(4.6, -9.88) * mm});
            skArc(sketch, "E234.1.0", {"start": v(3.19, -10.93) * mm, "mid": v(2.96, -10.64) * mm, "end": v(2.59, -10.59) * mm});
            skLineSegment(sketch, "E234.1.1", {"start": v(3.19, -10.93) * mm, "end": v(3.39, -11.62) * mm});
            skLineSegment(sketch, "E234.1.2", {"start": v(3.39, -11.62) * mm, "end": v(3.58, -11.56) * mm});
            skLineSegment(sketch, "E234.1.3", {"start": v(4.6, -9.88) * mm, "end": v(3.58, -11.56) * mm});
            skArc(sketch, "E234.2.0", {"start": v(1, -11.35) * mm, "mid": v(0.82, -11.01) * mm, "end": v(0.47, -10.89) * mm});
            skLineSegment(sketch, "E234.2.1", {"start": v(1, -11.35) * mm, "end": v(1.05, -12.05) * mm});
            skLineSegment(sketch, "E234.2.2", {"start": v(1.05, -12.05) * mm, "end": v(1.25, -12.04) * mm});
            skLineSegment(sketch, "E234.2.3", {"start": v(2.59, -10.59) * mm, "end": v(1.25, -12.04) * mm});
            skLineSegment(sketch, "E234.anchor1", {"start": v(0, 0) * mm, "end": v(4.82, -10.33) * mm, "construction": true});
            skLineSegment(sketch, "E234.anchor2", {"start": v(0, 0) * mm, "end": v(-10.33, -4.82) * mm, "construction": true});
            skLineSegment(sketch, "E235", {"start": v(6.4, -8.82) * mm, "end": v(7.2, -9.94) * mm, "construction": true});
            skLineSegment(sketch, "E236", {"start": v(5.76, -10.64) * mm, "end": v(6.4, -8.82) * mm});
            skArc(sketch, "E237.1.0", {"start": v(7.09, -8.91) * mm, "mid": v(6.77, -8.73) * mm, "end": v(6.4, -8.82) * mm});
            skLineSegment(sketch, "E237.1.1", {"start": v(7.09, -8.91) * mm, "end": v(7.53, -9.47) * mm});
            skLineSegment(sketch, "E237.1.2", {"start": v(7.53, -9.47) * mm, "end": v(7.69, -9.35) * mm});
            skLineSegment(sketch, "E237.1.3", {"start": v(7.69, -9.35) * mm, "end": v(7.97, -7.44) * mm});
            skLineSegment(sketch, "E237.anchor2", {"start": v(0, 0) * mm, "end": v(6.7, -9.22) * mm, "construction": true});
            skSolve(sketch);
        }
        {
            var Q0;
            {var subQ2=sQuery(id+"F18.wireOp",EDGE,"E237.1.0");Q0=makeQuery(id+"F18.imprint","IMPRINT",FACE,{"disambiguationData":[TD([[makeQuery(id+"F18.imprint","IMPRINT",EDGE,{"derivedFrom":subQ2}),-1.0]])]});}
            var Q1;
            Q1=makeQuery(id+"F18.imprint","IMPRINT",FACE,{"disambiguationData":[TD([[makeQuery(id+"F18.imprint","IMPRINT",EDGE,{"derivedFrom":sQuery(id+"F18.wireOp",EDGE,"E231")}),1.0]])]});
            var Q2;
            {var subQ1=sQuery(id+"F18.wireOp",EDGE,"E234.1.0");Q2=makeQuery(id+"F18.imprint","IMPRINT",FACE,{"disambiguationData":[TD([[makeQuery(id+"F18.imprint","IMPRINT",EDGE,{"derivedFrom":subQ1}),-1.0]])]});}
            var Q3;
            {var subQ2=sQuery(id+"F18.wireOp",EDGE,"E234.2.0");Q3=makeQuery(id+"F18.imprint","IMPRINT",FACE,{"disambiguationData":[TD([[makeQuery(id+"F18.imprint","IMPRINT",EDGE,{"derivedFrom":subQ2}),-1.0]])]});}
            var Q4;
            Q4=makeQuery(id+"F18.imprint","IMPRINT",FACE,{"disambiguationData":[TD([[makeQuery(id+"F18.imprint","IMPRINT",EDGE,{"derivedFrom":sQuery(id+"F18.wireOp",EDGE,"E213")}),-1.0]])]});
            extrude(context, id + "F19", {"entities" : qUnion([Q0, Q1, Q2, Q3, Q4]), "depth" : 1.5 * mm});
        }
        {
            var Q0;
            Q0=makeQuery(id+"F19.opExtrude","CAP_FACE",FACE,{"disambiguationData":[OSD([sQuery(id+"F18.wireOp",EDGE,"E212"),sQuery(id+"F18.wireOp",EDGE,"E213"),sQuery(id+"F18.wireOp",EDGE,"E214"),sQuery(id+"F18.wireOp",EDGE,"E217"),sQuery(id+"F18.wireOp",EDGE,"E218"),sQuery(id+"F18.wireOp",EDGE,"E219.trimOffspring"),sQuery(id+"F18.wireOp",EDGE,"E221"),sQuery(id+"F18.wireOp",EDGE,"E222"),sQuery(id+"F18.wireOp",EDGE,"E223"),sQuery(id+"F18.wireOp",EDGE,"E224"),sQuery(id+"F18.wireOp",EDGE,"E225"),sQuery(id+"F18.wireOp",EDGE,"E226"),sQuery(id+"F18.wireOp",EDGE,"E227"),sQuery(id+"F18.wireOp",EDGE,"E228"),sQuery(id+"F18.wireOp",EDGE,"E229.filletArc"),sQuery(id+"F18.wireOp",EDGE,"E231"),sQuery(id+"F18.wireOp",EDGE,"E232"),sQuery(id+"F18.wireOp",EDGE,"E233.filletArc"),sQuery(id+"F18.wireOp",EDGE,"E234.1.0"),sQuery(id+"F18.wireOp",EDGE,"E234.1.1"),sQuery(id+"F18.wireOp",EDGE,"E234.1.2"),sQuery(id+"F18.wireOp",EDGE,"E234.1.3"),sQuery(id+"F18.wireOp",EDGE,"E234.2.0"),sQuery(id+"F18.wireOp",EDGE,"E234.2.1"),sQuery(id+"F18.wireOp",EDGE,"E234.2.2"),sQuery(id+"F18.wireOp",EDGE,"E234.2.3"),sQuery(id+"F18.wireOp",EDGE,"E236"),sQuery(id+"F18.wireOp",EDGE,"E237.1.0"),sQuery(id+"F18.wireOp",EDGE,"E237.1.1"),sQuery(id+"F18.wireOp",EDGE,"E237.1.2"),sQuery(id+"F18.wireOp",EDGE,"E237.1.3")])],"isStart":false});
            var sketch = newSketch(context, id + "F20", { "sketchPlane" : qUnion([Q0])});
            skArc(sketch, "E238", {"start": v(9.11, -5.98) * mm, "mid": v(-0.55, -10.89) * mm, "end": v(-9.67, -5.03) * mm});
            skArc(sketch, "E239", {"start": v(-5, -7.84) * mm, "mid": v(0, -9.3) * mm, "end": v(5, -7.84) * mm});
            skArc(sketch, "E240", {"start": v(6.59, -6.42) * mm, "mid": v(5.83, -7.12) * mm, "end": v(5, -7.72) * mm});
            skLineSegment(sketch, "E241", {"start": v(9.97, -5.19) * mm, "end": v(0, 0) * mm, "construction": true});
            skLineSegment(sketch, "E242", {"start": v(-9.67, -5.03) * mm, "end": v(0, 0) * mm, "construction": true});
            skLineSegment(sketch, "E243", {"start": v(5, -7.84) * mm, "end": v(5, -7.72) * mm});
            skLineSegment(sketch, "E244", {"start": v(-5, -7.84) * mm, "end": v(-5, -7.72) * mm});
            skArc(sketch, "E245.trimOffspring", {"start": v(-5, -7.72) * mm, "mid": v(-5.83, -7.12) * mm, "end": v(-6.59, -6.42) * mm});
            skArc(sketch, "E246", {"start": v(-6.15, -3.75) * mm, "mid": v(0.86, -7.15) * mm, "end": v(6.86, -2.18) * mm, "construction": true});
            skLineSegment(sketch, "E247", {"start": v(-6.59, -6.42) * mm, "end": v(-5.54, -4.6) * mm});
            skLineSegment(sketch, "E248", {"start": v(6.59, -6.42) * mm, "end": v(5.54, -4.6) * mm});
            skArc(sketch, "E249", {"start": v(-5.54, -4.6) * mm, "mid": v(-5.68, -4.43) * mm, "end": v(-5.81, -4.25) * mm});
            skLineSegment(sketch, "E250", {"start": v(-5.81, -4.25) * mm, "end": v(-8.16, -4.25) * mm});
            skLineSegment(sketch, "E251", {"start": v(-8.16, -4.25) * mm, "end": v(-9.67, -5.03) * mm});
            skArc(sketch, "E252", {"start": v(5.54, -4.6) * mm, "mid": v(5.68, -4.43) * mm, "end": v(5.81, -4.25) * mm});
            skLineSegment(sketch, "E253", {"start": v(5.81, -4.25) * mm, "end": v(8.16, -4.25) * mm});
            skLineSegment(sketch, "E254", {"start": v(8.16, -4.25) * mm, "end": v(8.74, -4.55) * mm});
            skArc(sketch, "E255.filletArc", {"start": v(9.11, -5.98) * mm, "mid": v(9.24, -5.18) * mm, "end": v(8.74, -4.55) * mm});
            skPoint(sketch, "E256.visualSharp", {"position": v(-9.67, -5.03) * mm});
            skLineSegment(sketch, "E257", {"start": v(5.26, -10.1) * mm, "end": v(5.59, -10.73) * mm});
            skLineSegment(sketch, "E258", {"start": v(5.59, -10.73) * mm, "end": v(5.76, -10.64) * mm});
            skPoint(sketch, "E259.newPointA", {"position": v(5.03, -9.67) * mm});
            skArc(sketch, "E259.filletArc", {"start": v(5.26, -10.1) * mm, "mid": v(4.98, -9.86) * mm, "end": v(4.6, -9.88) * mm});
            skArc(sketch, "E260.1.0", {"start": v(3.19, -10.93) * mm, "mid": v(2.96, -10.64) * mm, "end": v(2.59, -10.59) * mm});
            skLineSegment(sketch, "E260.1.1", {"start": v(3.19, -10.93) * mm, "end": v(3.39, -11.62) * mm});
            skLineSegment(sketch, "E260.1.2", {"start": v(3.39, -11.62) * mm, "end": v(3.58, -11.56) * mm});
            skLineSegment(sketch, "E260.1.3", {"start": v(4.6, -9.88) * mm, "end": v(3.58, -11.56) * mm});
            skLineSegment(sketch, "E260.anchor1", {"start": v(0, 0) * mm, "end": v(4.82, -10.33) * mm, "construction": true});
            skLineSegment(sketch, "E260.anchor2", {"start": v(0, 0) * mm, "end": v(-10.33, -4.82) * mm, "construction": true});
            skLineSegment(sketch, "E261", {"start": v(6.4, -8.82) * mm, "end": v(7.2, -9.94) * mm, "construction": true});
            skLineSegment(sketch, "E262", {"start": v(5.76, -10.64) * mm, "end": v(6.4, -8.82) * mm});
            skArc(sketch, "E263.1.0", {"start": v(7.09, -8.91) * mm, "mid": v(6.77, -8.73) * mm, "end": v(6.4, -8.82) * mm});
            skLineSegment(sketch, "E263.1.1", {"start": v(7.09, -8.91) * mm, "end": v(7.53, -9.47) * mm});
            skLineSegment(sketch, "E263.1.2", {"start": v(7.53, -9.47) * mm, "end": v(7.69, -9.35) * mm});
            skLineSegment(sketch, "E263.1.3", {"start": v(7.69, -9.35) * mm, "end": v(7.97, -7.44) * mm});
            skLineSegment(sketch, "E263.anchor2", {"start": v(0, 0) * mm, "end": v(6.7, -9.22) * mm, "construction": true});
            skSolve(sketch);
        }
        {
            var Q0;
            Q0 = qSketchRegion(id + "F20", true);
            extrude(context, id + "F21", {"entities" : qUnion([Q0]), "depth" : 1.5 * mm});
        }
        {
            var Q0;
            Q0=makeQuery(id+"F21.opExtrude","CAP_FACE",FACE,{"disambiguationData":[OSD([sQuery(id+"F20.wireOp",EDGE,"E238"),sQuery(id+"F20.wireOp",EDGE,"E239"),sQuery(id+"F20.wireOp",EDGE,"E240"),sQuery(id+"F20.wireOp",EDGE,"E243"),sQuery(id+"F20.wireOp",EDGE,"E244"),sQuery(id+"F20.wireOp",EDGE,"E245.trimOffspring"),sQuery(id+"F20.wireOp",EDGE,"E247"),sQuery(id+"F20.wireOp",EDGE,"E248"),sQuery(id+"F20.wireOp",EDGE,"E249"),sQuery(id+"F20.wireOp",EDGE,"E250"),sQuery(id+"F20.wireOp",EDGE,"E251"),sQuery(id+"F20.wireOp",EDGE,"E252"),sQuery(id+"F20.wireOp",EDGE,"E253"),sQuery(id+"F20.wireOp",EDGE,"E254"),sQuery(id+"F20.wireOp",EDGE,"E255.filletArc"),sQuery(id+"F20.wireOp",EDGE,"E257"),sQuery(id+"F20.wireOp",EDGE,"E258"),sQuery(id+"F20.wireOp",EDGE,"E259.filletArc"),sQuery(id+"F20.wireOp",EDGE,"E260.1.0"),sQuery(id+"F20.wireOp",EDGE,"E260.1.1"),sQuery(id+"F20.wireOp",EDGE,"E260.1.2"),sQuery(id+"F20.wireOp",EDGE,"E260.1.3"),sQuery(id+"F20.wireOp",EDGE,"E262"),sQuery(id+"F20.wireOp",EDGE,"E263.1.0"),sQuery(id+"F20.wireOp",EDGE,"E263.1.1"),sQuery(id+"F20.wireOp",EDGE,"E263.1.2"),sQuery(id+"F20.wireOp",EDGE,"E263.1.3")])],"isStart":false});
            var sketch = newSketch(context, id + "F22", { "sketchPlane" : qUnion([Q0])});
            skArc(sketch, "E264", {"start": v(9.11, -5.98) * mm, "mid": v(-0.55, -10.89) * mm, "end": v(-9.67, -5.03) * mm});
            skArc(sketch, "E265", {"start": v(-5, -7.84) * mm, "mid": v(0, -9.3) * mm, "end": v(5, -7.84) * mm});
            skArc(sketch, "E266", {"start": v(6.59, -6.42) * mm, "mid": v(5.83, -7.12) * mm, "end": v(5, -7.72) * mm});
            skLineSegment(sketch, "E267", {"start": v(9.97, -5.19) * mm, "end": v(0, 0) * mm, "construction": true});
            skLineSegment(sketch, "E268", {"start": v(-9.67, -5.03) * mm, "end": v(0, 0) * mm, "construction": true});
            skLineSegment(sketch, "E269", {"start": v(5, -7.84) * mm, "end": v(5, -7.72) * mm});
            skLineSegment(sketch, "E270", {"start": v(-5, -7.84) * mm, "end": v(-5, -7.72) * mm});
            skArc(sketch, "E271.trimOffspring", {"start": v(-5, -7.72) * mm, "mid": v(-5.83, -7.12) * mm, "end": v(-6.59, -6.42) * mm});
            skArc(sketch, "E272", {"start": v(-6.15, -3.75) * mm, "mid": v(0.86, -7.15) * mm, "end": v(6.86, -2.18) * mm, "construction": true});
            skLineSegment(sketch, "E273", {"start": v(-6.59, -6.42) * mm, "end": v(-5.54, -4.6) * mm});
            skLineSegment(sketch, "E274", {"start": v(6.59, -6.42) * mm, "end": v(5.54, -4.6) * mm});
            skArc(sketch, "E275", {"start": v(-5.54, -4.6) * mm, "mid": v(-5.68, -4.43) * mm, "end": v(-5.81, -4.25) * mm});
            skLineSegment(sketch, "E276", {"start": v(-5.81, -4.25) * mm, "end": v(-8.16, -4.25) * mm});
            skLineSegment(sketch, "E277", {"start": v(-8.16, -4.25) * mm, "end": v(-9.67, -5.03) * mm});
            skArc(sketch, "E278", {"start": v(5.54, -4.6) * mm, "mid": v(5.68, -4.43) * mm, "end": v(5.81, -4.25) * mm});
            skLineSegment(sketch, "E279", {"start": v(5.81, -4.25) * mm, "end": v(8.16, -4.25) * mm});
            skLineSegment(sketch, "E280", {"start": v(8.16, -4.25) * mm, "end": v(8.74, -4.55) * mm});
            skArc(sketch, "E281.filletArc", {"start": v(9.11, -5.98) * mm, "mid": v(9.24, -5.18) * mm, "end": v(8.74, -4.55) * mm});
            skPoint(sketch, "E282.visualSharp", {"position": v(-9.67, -5.03) * mm});
            skLineSegment(sketch, "E283", {"start": v(5.26, -10.1) * mm, "end": v(5.59, -10.73) * mm});
            skLineSegment(sketch, "E284", {"start": v(5.59, -10.73) * mm, "end": v(5.76, -10.64) * mm});
            skPoint(sketch, "E285.newPointA", {"position": v(5.03, -9.67) * mm});
            skArc(sketch, "E285.filletArc", {"start": v(5.26, -10.1) * mm, "mid": v(4.98, -9.86) * mm, "end": v(4.6, -9.88) * mm});
            skLineSegment(sketch, "E286.anchor1", {"start": v(0, 0) * mm, "end": v(4.82, -10.33) * mm, "construction": true});
            skLineSegment(sketch, "E286.anchor2", {"start": v(0, 0) * mm, "end": v(-10.33, -4.82) * mm, "construction": true});
            skLineSegment(sketch, "E287", {"start": v(6.4, -8.82) * mm, "end": v(7.2, -9.94) * mm, "construction": true});
            skLineSegment(sketch, "E288", {"start": v(5.76, -10.64) * mm, "end": v(6.4, -8.82) * mm});
            skArc(sketch, "E289.1.0", {"start": v(7.09, -8.91) * mm, "mid": v(6.77, -8.73) * mm, "end": v(6.4, -8.82) * mm});
            skLineSegment(sketch, "E289.1.1", {"start": v(7.09, -8.91) * mm, "end": v(7.53, -9.47) * mm});
            skLineSegment(sketch, "E289.1.2", {"start": v(7.53, -9.47) * mm, "end": v(7.69, -9.35) * mm});
            skLineSegment(sketch, "E289.1.3", {"start": v(7.69, -9.35) * mm, "end": v(7.97, -7.44) * mm});
            skLineSegment(sketch, "E289.anchor2", {"start": v(0, 0) * mm, "end": v(6.7, -9.22) * mm, "construction": true});
            skSolve(sketch);
        }
        {
            var Q0;
            Q0 = qSketchRegion(id + "F22", true);
            extrude(context, id + "F23", {"entities" : qUnion([Q0]), "depth" : 1.5 * mm});
        }
        {
            var Q0;
            Q0=makeQuery(id+"F23.opExtrude","CAP_FACE",FACE,{"disambiguationData":[OSD([sQuery(id+"F22.wireOp",EDGE,"E264"),sQuery(id+"F22.wireOp",EDGE,"E265"),sQuery(id+"F22.wireOp",EDGE,"E266"),sQuery(id+"F22.wireOp",EDGE,"E269"),sQuery(id+"F22.wireOp",EDGE,"E270"),sQuery(id+"F22.wireOp",EDGE,"E271.trimOffspring"),sQuery(id+"F22.wireOp",EDGE,"E273"),sQuery(id+"F22.wireOp",EDGE,"E274"),sQuery(id+"F22.wireOp",EDGE,"E275"),sQuery(id+"F22.wireOp",EDGE,"E276"),sQuery(id+"F22.wireOp",EDGE,"E277"),sQuery(id+"F22.wireOp",EDGE,"E278"),sQuery(id+"F22.wireOp",EDGE,"E279"),sQuery(id+"F22.wireOp",EDGE,"E280"),sQuery(id+"F22.wireOp",EDGE,"E281.filletArc"),sQuery(id+"F22.wireOp",EDGE,"E283"),sQuery(id+"F22.wireOp",EDGE,"E284"),sQuery(id+"F22.wireOp",EDGE,"E285.filletArc"),sQuery(id+"F22.wireOp",EDGE,"E288"),sQuery(id+"F22.wireOp",EDGE,"E289.1.0"),sQuery(id+"F22.wireOp",EDGE,"E289.1.1"),sQuery(id+"F22.wireOp",EDGE,"E289.1.2"),sQuery(id+"F22.wireOp",EDGE,"E289.1.3")])],"isStart":false});
            var sketch = newSketch(context, id + "F24", { "sketchPlane" : qUnion([Q0])});
            skArc(sketch, "E290", {"start": v(9.11, -5.98) * mm, "mid": v(-0.55, -10.89) * mm, "end": v(-9.67, -5.03) * mm});
            skArc(sketch, "E291", {"start": v(-5, -7.84) * mm, "mid": v(0, -9.3) * mm, "end": v(5, -7.84) * mm});
            skArc(sketch, "E292", {"start": v(6.59, -6.42) * mm, "mid": v(5.83, -7.12) * mm, "end": v(5, -7.72) * mm});
            skLineSegment(sketch, "E293", {"start": v(9.97, -5.19) * mm, "end": v(0, 0) * mm, "construction": true});
            skLineSegment(sketch, "E294", {"start": v(-9.67, -5.03) * mm, "end": v(0, 0) * mm, "construction": true});
            skLineSegment(sketch, "E295", {"start": v(5, -7.84) * mm, "end": v(5, -7.72) * mm});
            skLineSegment(sketch, "E296", {"start": v(-5, -7.84) * mm, "end": v(-5, -7.72) * mm});
            skArc(sketch, "E297.trimOffspring", {"start": v(-5, -7.72) * mm, "mid": v(-5.83, -7.12) * mm, "end": v(-6.59, -6.42) * mm});
            skArc(sketch, "E298", {"start": v(-6.15, -3.75) * mm, "mid": v(0.86, -7.15) * mm, "end": v(6.86, -2.18) * mm, "construction": true});
            skLineSegment(sketch, "E299", {"start": v(-6.59, -6.42) * mm, "end": v(-5.54, -4.6) * mm});
            skLineSegment(sketch, "E300", {"start": v(6.59, -6.42) * mm, "end": v(5.54, -4.6) * mm});
            skArc(sketch, "E301", {"start": v(-5.54, -4.6) * mm, "mid": v(-5.68, -4.43) * mm, "end": v(-5.81, -4.25) * mm});
            skLineSegment(sketch, "E302", {"start": v(-5.81, -4.25) * mm, "end": v(-8.16, -4.25) * mm});
            skLineSegment(sketch, "E303", {"start": v(-8.16, -4.25) * mm, "end": v(-9.67, -5.03) * mm});
            skArc(sketch, "E304", {"start": v(5.54, -4.6) * mm, "mid": v(5.68, -4.43) * mm, "end": v(5.81, -4.25) * mm});
            skLineSegment(sketch, "E305", {"start": v(5.81, -4.25) * mm, "end": v(8.16, -4.25) * mm});
            skLineSegment(sketch, "E306", {"start": v(8.16, -4.25) * mm, "end": v(8.74, -4.55) * mm});
            skArc(sketch, "E307.filletArc", {"start": v(9.11, -5.98) * mm, "mid": v(9.24, -5.18) * mm, "end": v(8.74, -4.55) * mm});
            skPoint(sketch, "E308.visualSharp", {"position": v(-9.67, -5.03) * mm});
            skPoint(sketch, "E309.newPointA", {"position": v(5.03, -9.67) * mm});
            skLineSegment(sketch, "E310.anchor1", {"start": v(0, 0) * mm, "end": v(4.82, -10.33) * mm, "construction": true});
            skLineSegment(sketch, "E310.anchor2", {"start": v(0, 0) * mm, "end": v(-10.33, -4.82) * mm, "construction": true});
            skLineSegment(sketch, "E311", {"start": v(6.4, -8.82) * mm, "end": v(7.2, -9.94) * mm, "construction": true});
            skArc(sketch, "E312.1.0", {"start": v(7.09, -8.91) * mm, "mid": v(6.77, -8.73) * mm, "end": v(6.4, -8.82) * mm});
            skLineSegment(sketch, "E312.1.1", {"start": v(7.09, -8.91) * mm, "end": v(7.53, -9.47) * mm});
            skLineSegment(sketch, "E312.1.2", {"start": v(7.53, -9.47) * mm, "end": v(7.69, -9.35) * mm});
            skLineSegment(sketch, "E312.1.3", {"start": v(7.69, -9.35) * mm, "end": v(7.97, -7.44) * mm});
            skLineSegment(sketch, "E312.anchor2", {"start": v(0, 0) * mm, "end": v(6.7, -9.22) * mm, "construction": true});
            skSolve(sketch);
        }
        {
            var Q0;
            Q0 = qSketchRegion(id + "F24", true);
            extrude(context, id + "F25", {"entities" : qUnion([Q0]), "depth" : 1.5 * mm});
        }
        {
            var Q0;
            Q0=makeQuery(id+"F25.opExtrude","CAP_FACE",FACE,{"disambiguationData":[OSD([sQuery(id+"F24.wireOp",EDGE,"E290"),sQuery(id+"F24.wireOp",EDGE,"E291"),sQuery(id+"F24.wireOp",EDGE,"E292"),sQuery(id+"F24.wireOp",EDGE,"E295"),sQuery(id+"F24.wireOp",EDGE,"E296"),sQuery(id+"F24.wireOp",EDGE,"E297.trimOffspring"),sQuery(id+"F24.wireOp",EDGE,"E299"),sQuery(id+"F24.wireOp",EDGE,"E300"),sQuery(id+"F24.wireOp",EDGE,"E301"),sQuery(id+"F24.wireOp",EDGE,"E302"),sQuery(id+"F24.wireOp",EDGE,"E303"),sQuery(id+"F24.wireOp",EDGE,"E304"),sQuery(id+"F24.wireOp",EDGE,"E305"),sQuery(id+"F24.wireOp",EDGE,"E306"),sQuery(id+"F24.wireOp",EDGE,"E307.filletArc"),sQuery(id+"F24.wireOp",EDGE,"E312.1.0"),sQuery(id+"F24.wireOp",EDGE,"E312.1.1"),sQuery(id+"F24.wireOp",EDGE,"E312.1.2"),sQuery(id+"F24.wireOp",EDGE,"E312.1.3")])],"isStart":false});
            cPlane(context, id + "F26", {"entities" : qUnion([Q0]), "cplaneType" : CPlaneType.OFFSET, "offset" : 10 * mm, "width" : 150 * mm, "height" : 150 * mm});
        }
        {
            var Q0;
            Q0=qCreatedBy(id+"F26.planeOp",FACE);
            var sketch = newSketch(context, id + "F27", { "sketchPlane" : qUnion([Q0])});
            skArc(sketch, "E313", {"start": v(9.11, -5.98) * mm, "mid": v(-0.55, -10.89) * mm, "end": v(-9.67, -5.03) * mm});
            skArc(sketch, "E314", {"start": v(-5, -7.84) * mm, "mid": v(0, -9.3) * mm, "end": v(5, -7.84) * mm});
            skArc(sketch, "E315", {"start": v(6.59, -6.42) * mm, "mid": v(5.83, -7.12) * mm, "end": v(5, -7.72) * mm});
            skLineSegment(sketch, "E316", {"start": v(9.97, -5.19) * mm, "end": v(0, 0) * mm, "construction": true});
            skLineSegment(sketch, "E317", {"start": v(-9.67, -5.03) * mm, "end": v(0, 0) * mm, "construction": true});
            skLineSegment(sketch, "E318", {"start": v(5, -7.84) * mm, "end": v(5, -7.72) * mm});
            skLineSegment(sketch, "E319", {"start": v(-5, -7.84) * mm, "end": v(-5, -7.72) * mm});
            skArc(sketch, "E320.trimOffspring", {"start": v(-5, -7.72) * mm, "mid": v(-5.83, -7.12) * mm, "end": v(-6.59, -6.42) * mm});
            skArc(sketch, "E321", {"start": v(-6.15, -3.75) * mm, "mid": v(0.86, -7.15) * mm, "end": v(6.86, -2.18) * mm, "construction": true});
            skLineSegment(sketch, "E322", {"start": v(-6.59, -6.42) * mm, "end": v(-5.54, -4.6) * mm});
            skLineSegment(sketch, "E323", {"start": v(6.59, -6.42) * mm, "end": v(5.54, -4.6) * mm});
            skArc(sketch, "E324", {"start": v(-5.54, -4.6) * mm, "mid": v(-5.68, -4.43) * mm, "end": v(-5.81, -4.25) * mm});
            skLineSegment(sketch, "E325", {"start": v(-5.81, -4.25) * mm, "end": v(-8.16, -4.25) * mm});
            skLineSegment(sketch, "E326", {"start": v(-8.16, -4.25) * mm, "end": v(-9.67, -5.03) * mm});
            skArc(sketch, "E327", {"start": v(5.54, -4.6) * mm, "mid": v(5.68, -4.43) * mm, "end": v(5.81, -4.25) * mm});
            skLineSegment(sketch, "E328", {"start": v(5.81, -4.25) * mm, "end": v(8.16, -4.25) * mm});
            skLineSegment(sketch, "E329", {"start": v(8.16, -4.25) * mm, "end": v(8.74, -4.55) * mm});
            skArc(sketch, "E330.filletArc", {"start": v(9.11, -5.98) * mm, "mid": v(9.24, -5.18) * mm, "end": v(8.74, -4.55) * mm});
            skPoint(sketch, "E331.visualSharp", {"position": v(-9.67, -5.03) * mm});
            skPoint(sketch, "E332.newPointA", {"position": v(5.03, -9.67) * mm});
            skLineSegment(sketch, "E333.anchor1", {"start": v(0, 0) * mm, "end": v(4.82, -10.33) * mm, "construction": true});
            skLineSegment(sketch, "E333.anchor2", {"start": v(0, 0) * mm, "end": v(-10.33, -4.82) * mm, "construction": true});
            skLineSegment(sketch, "E334", {"start": v(6.4, -8.82) * mm, "end": v(7.2, -9.94) * mm, "construction": true});
            skArc(sketch, "E335.1.0", {"start": v(7.09, -8.91) * mm, "mid": v(6.77, -8.73) * mm, "end": v(6.4, -8.82) * mm});
            skLineSegment(sketch, "E335.1.1", {"start": v(7.09, -8.91) * mm, "end": v(7.53, -9.47) * mm});
            skLineSegment(sketch, "E335.1.2", {"start": v(7.53, -9.47) * mm, "end": v(7.69, -9.35) * mm});
            skLineSegment(sketch, "E335.1.3", {"start": v(7.69, -9.35) * mm, "end": v(7.97, -7.44) * mm});
            skLineSegment(sketch, "E335.anchor2", {"start": v(0, 0) * mm, "end": v(6.7, -9.22) * mm, "construction": true});
            skSolve(sketch);
        }
        {
            var Q0;
            Q0=makeQuery(id+"F27.imprint","IMPRINT",FACE,{"disambiguationData":[TD([[makeQuery(id+"F27.imprint","IMPRINT",EDGE,{"derivedFrom":sQuery(id+"F27.wireOp",EDGE,"E314")}),-1.0]])]});
            var Q1;
            {var subQ2=sQuery(id+"F27.wireOp",EDGE,"E335.1.0");Q1=makeQuery(id+"F27.imprint","IMPRINT",FACE,{"disambiguationData":[TD([[makeQuery(id+"F27.imprint","IMPRINT",EDGE,{"derivedFrom":subQ2}),-1.0]])]});}
            extrude(context, id + "F28", {"entities" : qUnion([Q0, Q1]), "depth" : 1 * mm});
        }
        {
            var Q0;
            Q0=makeQuery(id+"F28.opExtrude","CAP_FACE",FACE,{"disambiguationData":[OSD([sQuery(id+"F27.wireOp",EDGE,"E313"),sQuery(id+"F27.wireOp",EDGE,"E314"),sQuery(id+"F27.wireOp",EDGE,"E315"),sQuery(id+"F27.wireOp",EDGE,"E318"),sQuery(id+"F27.wireOp",EDGE,"E319"),sQuery(id+"F27.wireOp",EDGE,"E320.trimOffspring"),sQuery(id+"F27.wireOp",EDGE,"E322"),sQuery(id+"F27.wireOp",EDGE,"E323"),sQuery(id+"F27.wireOp",EDGE,"E324"),sQuery(id+"F27.wireOp",EDGE,"E325"),sQuery(id+"F27.wireOp",EDGE,"E326"),sQuery(id+"F27.wireOp",EDGE,"E327"),sQuery(id+"F27.wireOp",EDGE,"E328"),sQuery(id+"F27.wireOp",EDGE,"E329"),sQuery(id+"F27.wireOp",EDGE,"E330.filletArc"),sQuery(id+"F27.wireOp",EDGE,"E335.1.0"),sQuery(id+"F27.wireOp",EDGE,"E335.1.1"),sQuery(id+"F27.wireOp",EDGE,"E335.1.2"),sQuery(id+"F27.wireOp",EDGE,"E335.1.3")])],"isStart":true});
            var sketch = newSketch(context, id + "F29", { "sketchPlane" : qUnion([Q0])});
            skArc(sketch, "E336", {"start": v(9.67, -5.03) * mm, "mid": v(0, -10.9) * mm, "end": v(-9.67, -5.03) * mm});
            skLineSegment(sketch, "E337", {"start": v(9.97, -5.19) * mm, "end": v(0, 0) * mm, "construction": true});
            skLineSegment(sketch, "E338", {"start": v(-9.67, -5.03) * mm, "end": v(0, 0) * mm, "construction": true});
            skArc(sketch, "E339", {"start": v(-6.15, -3.75) * mm, "mid": v(0.86, -7.15) * mm, "end": v(6.86, -2.18) * mm, "construction": true});
            skLineSegment(sketch, "E340", {"start": v(-5.81, -4.25) * mm, "end": v(-8.16, -4.25) * mm});
            skLineSegment(sketch, "E341", {"start": v(-8.16, -4.25) * mm, "end": v(-9.67, -5.03) * mm});
            skArc(sketch, "E342", {"start": v(-5.81, -4.25) * mm, "mid": v(0, -7.2) * mm, "end": v(5.81, -4.25) * mm});
            skLineSegment(sketch, "E343", {"start": v(5.81, -4.25) * mm, "end": v(8.16, -4.25) * mm});
            skLineSegment(sketch, "E344", {"start": v(8.16, -4.25) * mm, "end": v(9.67, -5.03) * mm});
            skPoint(sketch, "E345.visualSharp", {"position": v(-9.67, -5.03) * mm});
            skPoint(sketch, "E346.newPointA", {"position": v(5.03, -9.67) * mm});
            skLineSegment(sketch, "E347.anchor1", {"start": v(0, 0) * mm, "end": v(4.82, -10.33) * mm, "construction": true});
            skLineSegment(sketch, "E347.anchor2", {"start": v(0, 0) * mm, "end": v(-10.33, -4.82) * mm, "construction": true});
            skArc(sketch, "E348", {"start": v(7.27, -3.79) * mm, "mid": v(0, -8.2) * mm, "end": v(-7.27, -3.79) * mm, "construction": true});
            skCircle(sketch, "E349", {"center": v(0, -8.2) * mm, "radius": 0.75 * mm});
            skCircle(sketch, "E350", {"center": v(5.3, -6.26) * mm, "radius": 0.75 * mm});
            skCircle(sketch, "E351", {"center": v(-5.3, -6.26) * mm, "radius": 0.75 * mm});
            skLineSegment(sketch, "E352.MirrorCS", {"start": v(8.16, 4.25) * mm, "end": v(9.67, 5.03) * mm});
            skLineSegment(sketch, "E353.MirrorCS", {"start": v(-5.81, 4.25) * mm, "end": v(-8.16, 4.25) * mm});
            skLineSegment(sketch, "E354.MirrorCS", {"start": v(-8.16, 4.25) * mm, "end": v(-9.67, 5.03) * mm});
            skPoint(sketch, "E355.MirrorP", {"position": v(5.03, 9.67) * mm});
            skCircle(sketch, "E356.MirrorC", {"center": v(5.3, 6.26) * mm, "radius": 0.75 * mm});
            skPoint(sketch, "E357.MirrorP", {"position": v(-9.67, 5.03) * mm});
            skCircle(sketch, "E358.MirrorC", {"center": v(0, 8.2) * mm, "radius": 0.75 * mm});
            skArc(sketch, "E359.MirrorCS", {"start": v(9.67, 5.03) * mm, "mid": v(0, 10.9) * mm, "end": v(-9.67, 5.03) * mm});
            skArc(sketch, "E360.MirrorCS", {"start": v(-5.81, 4.25) * mm, "mid": v(0, 7.2) * mm, "end": v(5.81, 4.25) * mm});
            skCircle(sketch, "E361.MirrorC", {"center": v(-5.3, 6.26) * mm, "radius": 0.75 * mm});
            skLineSegment(sketch, "E362.MirrorCS", {"start": v(5.81, 4.25) * mm, "end": v(8.16, 4.25) * mm});
            skSolve(sketch);
        }
        {
            var Q0;
            {var subQ0=makeQuery(id+"F28.opExtrude","CAP_EDGE",EDGE,{"disambiguationData":[OSD([sQuery(id+"F27.wireOp",EDGE,"E330.filletArc")])],"isStart":true});Q0=makeQuery(id+"F29.imprint","IMPRINT",FACE,{"disambiguationData":[TD([[makeQuery(id+"F29.imprint","IMPRINT",EDGE,{"derivedFrom":subQ0}),1.0]])]});}
            var Q1;
            {var subQ10=sQuery(id+"F29.wireOp",EDGE,"E353.MirrorCS");Q1=makeQuery(id+"F29.imprint","IMPRINT",FACE,{"disambiguationData":[TD([[makeQuery(id+"F29.imprint","IMPRINT",EDGE,{"derivedFrom":subQ10}),-1.0]])]});}
            var Q2;
            Q2=makeQuery(id+"F29.imprint","IMPRINT",FACE,{"disambiguationData":[TD([[makeQuery(id+"F29.imprint","IMPRINT",EDGE,{"derivedFrom":sQuery(id+"F29.wireOp",EDGE,"E356.MirrorC")}),1.0]])]});
            extrude(context, id + "F30", {"entities" : qUnion([Q0, Q1, Q2]), "operationType" : NewBodyOperationType.ADD, "depth" : 1 * mm});
        }
    });
